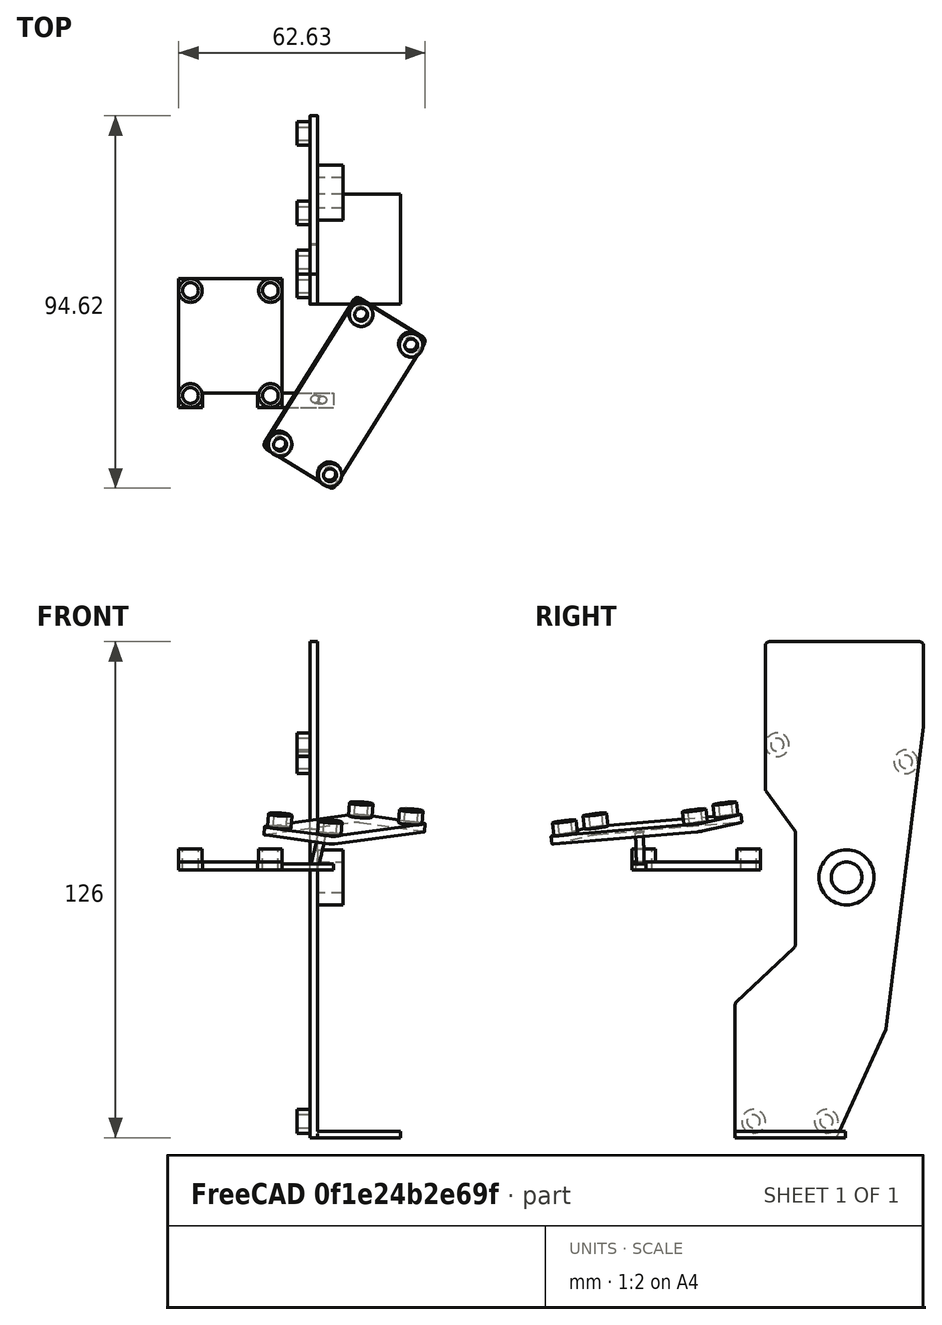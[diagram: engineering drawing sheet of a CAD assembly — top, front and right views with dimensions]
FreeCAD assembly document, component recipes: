
FREECAD ASSEMBLY — COMPONENT RECIPES ("case-vertical")

This assembly document has 10 components, labeled P0..P9 below (a component is one placed body or linked part). 8 of them carry a construction recipe — the FreeCAD feature program that regenerates the part from scratch, quoted from this document or its linked companion documents; the rest are supplied as boundary geometry only. No exploded tour is included for this assembly.
COMPONENT P0 — geometry summary ("Joystick v6"; no construction recipe available for this part):
  bounding box: 33.2 x 26.8 x 24.7 mm
  tessellated surface: 35,946 triangles
  volume: 4886 mm^3 (22% of its bounding box)
COMPONENT P1 — recipe-attached ("Part001", modeled in this document).
Construction recipe (the document's own serialized feature program — sketch geometry with constraints, then the solid features built on it; lengths are millimeters unless a unit is written):

FEATURE [Sketcher::SketchObject] PCB_Sketch_f9e4  label="left"
  ArcFitTolerance = 1e-06
  FullyConstrained = false
  MakeInternals = false
  MapMode = 5
  Placement = pos=(0,0,0) rot=(0,-1,0;1.5708rad)
  sketch-geometry (21):
    g0: LineSegment StartX=48.9342 StartY=15.25 StartZ=0 EndX=77.5946 EndY=15.25 EndZ=0
    g1: LineSegment StartX=27.2503 StartY=38.2054 StartZ=0 EndX=0.583058 EndY=26.0175 EndZ=0
    g2: LineSegment StartX=126 StartY=8.65 StartZ=0 EndX=126 EndY=45.95 EndZ=0
    g3: LineSegment StartX=9e-16 StartY=25.1085 StartZ=0 EndX=0 EndY=1 EndZ=0
    g4: LineSegment StartX=104.439 StartY=47.8424 StartZ=0 EndX=27.5489 EndY=38.289 EndZ=0
    g5: LineSegment StartX=34.5465 StartY=0.317255 StartZ=0 EndX=48.2035 EndY=14.9327 EndZ=0
    g6: LineSegment StartX=104.562 StartY=47.85 StartZ=0 EndX=125 EndY=47.85 EndZ=0
    g7: LineSegment StartX=125 StartY=7.65 StartZ=0 EndX=88.6266 EndY=7.65 EndZ=0
    g8: LineSegment StartX=1 StartY=1e-16 StartZ=0 EndX=33.8158 EndY=-1.6e-15 EndZ=0
    g9: LineSegment StartX=126 StartY=45.95 StartZ=0 EndX=126 EndY=46.85 EndZ=0
    g10: LineSegment StartX=78.291 StartY=14.9676 StartZ=0 EndX=88.0364 EndY=7.84274 EndZ=0
    g11: ArcOfCircle CenterX=27.666 CenterY=37.2959 CenterZ=0 NormalX=0 NormalY=0 NormalZ=-1 AngleXU=1.14211 Radius=1.00001 StartAngle=0 EndAngle=0.311303
    g12: ArcOfCircle CenterX=33.8158 CenterY=1.00002 CenterZ=0 NormalX=0 NormalY=0 NormalZ=-1 AngleXU=-2.39007 Radius=1.00002 StartAngle=0 EndAngle=0.81927
    g13: ArcOfCircle CenterX=48.9342 CenterY=14.25 CenterZ=0 NormalX=0 NormalY=0 NormalZ=-1 AngleXU=0.75152 Radius=1.00002 StartAngle=0 EndAngle=0.81927
    g14: ArcOfCircle CenterX=125 CenterY=46.85 CenterZ=0 NormalX=0 NormalY=0 NormalZ=-1 AngleXU=1.5708 Radius=0.999999 StartAngle=0 EndAngle=1.5708
    g15: ArcOfCircle CenterX=125 CenterY=8.65 CenterZ=0 NormalX=0 NormalY=0 NormalZ=-1 AngleXU=3.14159 Radius=0.999999 StartAngle=0 EndAngle=1.5708
    g16: ArcOfCircle CenterX=88.6266 CenterY=8.65 CenterZ=0 NormalX=0 NormalY=0 NormalZ=-1 AngleXU=-1.57079 Radius=1 StartAngle=0 EndAngle=0.631296
    g17: ArcOfCircle CenterX=104.562 CenterY=46.8498 CenterZ=0 NormalX=0 NormalY=0 NormalZ=-1 AngleXU=1.44719 Radius=1.00016 StartAngle=0 EndAngle=0.123594
    g18: ArcOfCircle CenterX=0.999999 CenterY=0.999999 CenterZ=0 NormalX=0 NormalY=0 NormalZ=-1 AngleXU=-1.5708 Radius=0.999999 StartAngle=0 EndAngle=1.5708
    g19: ArcOfCircle CenterX=1.00007 CenterY=25.1085 CenterZ=0 NormalX=0 NormalY=0 NormalZ=-1 AngleXU=4.52044e-05 Radius=1.00007 StartAngle=0 EndAngle=1.14063
    g20: ArcOfCircle CenterX=77.5946 CenterY=14.25 CenterZ=0 NormalX=0 NormalY=0 NormalZ=-1 AngleXU=1.57078 Radius=0.999961 StartAngle=0 EndAngle=0.770416
  constraints (21):
    c: Coincident(g3,g18)
    c: Coincident(g3,g19)
    c: Coincident(g1,g19)
    c: Coincident(g8,g18)
    c: Coincident(g1,g11)
    c: Coincident(g4,g11)
    c: Coincident(g8,g12)
    c: Coincident(g5,g12)
    c: Coincident(g5,g13)
    c: Coincident(g0,g13)
    c: Coincident(g0,g20)
    c: Coincident(g10,g20)
    c: Coincident(g10,g16)
    c: Coincident(g7,g16)
    c: Coincident(g4,g17)
    c: Coincident(g6,g17)
    c: Coincident(g7,g15)
    c: Coincident(g6,g14)
    c: Coincident(g2,g15)
    c: Coincident(g2,g9)
    c: Coincident(g9,g14)
FEATURE [PartDesign::Pad] Pad
  Direction = (-1,0,2e-16)
  Length = 2
  Length2 = 10
  Placement = pos=(0,0,0) rot=(0,-1,0;1.5708rad)
  Profile = -> PCB_Sketch_f9e4
  ReferenceAxis = -> PCB_Sketch_f9e4 [N_Axis]
  Refine = true
  Suppressed = false
  Type = 0
FEATURE [Sketcher::SketchObject] PCB_Sketch_f9e005  label="left holes"
  ArcFitTolerance = 1e-06
  AttachmentSupport = -> [Pad]
  FullyConstrained = false
  MakeInternals = false
  MapMode = 5
  Placement = pos=(-2,0,4e-16) rot=(0,-1,0;1.5708rad)
  sketch-geometry (8):
    g0: Circle CenterX=4.15 CenterY=23.1667 CenterZ=0 NormalX=0 NormalY=0 NormalZ=1 AngleXU=0 Radius=3
    g1: Circle CenterX=4.15 CenterY=4.65 CenterZ=0 NormalX=0 NormalY=0 NormalZ=1 AngleXU=0 Radius=3
    g2: Circle CenterX=95.5 CenterY=43.35 CenterZ=0 NormalX=0 NormalY=0 NormalZ=1 AngleXU=0 Radius=3
    g3: Circle CenterX=99.8333 CenterY=10.6833 CenterZ=0 NormalX=0 NormalY=0 NormalZ=1 AngleXU=0 Radius=3
    g4: Circle CenterX=95.5 CenterY=43.35 CenterZ=0 NormalX=0 NormalY=0 NormalZ=1 AngleXU=0 Radius=1.65
    g5: Circle CenterX=99.8333 CenterY=10.6833 CenterZ=0 NormalX=0 NormalY=0 NormalZ=1 AngleXU=0 Radius=1.65
    g6: Circle CenterX=4.15 CenterY=23.1667 CenterZ=0 NormalX=0 NormalY=0 NormalZ=1 AngleXU=0 Radius=1.65
    g7: Circle CenterX=4.15 CenterY=4.65 CenterZ=0 NormalX=0 NormalY=0 NormalZ=1 AngleXU=0 Radius=1.65
  constraints (12):
    c: Diameter(g0) = 6
    c: Diameter(g1) = 6
    c: Diameter(g2) = 6
    c: Diameter(g3) = 6
    c: Diameter(g4) = 3.3
    c: Coincident(g4,g2)
    c: Diameter(g5) = 3.3
    c: Coincident(g5,g3)
    c: Diameter(g6) = 3.3
    c: Coincident(g6,g0)
    c: Diameter(g7) = 3.3
    c: Coincident(g7,g1)
FEATURE [PartDesign::Pad] Pad003
  BaseFeature = -> Pad
  Direction = (-1,0,2e-16)
  Length = 3.3
  Length2 = 10
  Placement = pos=(0,0,0) rot=(0,-1,0;1.5708rad)
  Profile = -> PCB_Sketch_f9e005
  ReferenceAxis = -> PCB_Sketch_f9e005 [N_Axis]
  Refine = true
  Suppressed = false
  Type = 0
FEATURE [Sketcher::SketchObject] Sketch  label="tindie"
  ArcFitTolerance = 1e-06
  AttachmentSupport = -> [XY_Plane001]
  FullyConstrained = true
  MakeInternals = false
  MapMode = 5
  sketch-geometry (4):
    g0: LineSegment StartX=0 StartY=0 StartZ=0 EndX=21 EndY=0 EndZ=0
    g1: LineSegment StartX=21 StartY=0 StartZ=0 EndX=21 EndY=28 EndZ=0
    g2: LineSegment StartX=21 StartY=28 StartZ=0 EndX=0 EndY=28 EndZ=0
    g3: LineSegment StartX=0 StartY=28 StartZ=0 EndX=0 EndY=0 EndZ=0
  constraints (11):
    c: Coincident(g0,g1)
    c: Coincident(g1,g2)
    c: Coincident(g2,g3)
    c: Coincident(g3,g0)
    c: Horizontal(g0)
    c: Horizontal(g2)
    c: Vertical(g1)
    c: Vertical(g3)
    c: Coincident(g0,g-1)
    c: DistanceY(g1,g1) = 28
    c: DistanceX(g2,g2) = 21
FEATURE [Sketcher::SketchObject] PCB_Sketch_58ce002  label="thumb"
  ArcFitTolerance = 1e-06
  FullyConstrained = false
  MakeInternals = false
  sketch-geometry (8):
    g0: LineSegment StartX=21 StartY=44 StartZ=0 EndX=21 EndY=1 EndZ=0
    g1: LineSegment StartX=20 StartY=1e-16 StartZ=0 EndX=1 EndY=0 EndZ=0
    g2: LineSegment StartX=1 StartY=45 StartZ=0 EndX=20 EndY=45 EndZ=0
    g3: LineSegment StartX=1e-16 StartY=1 StartZ=0 EndX=3.3e-15 EndY=44 EndZ=0
    g4: ArcOfCircle CenterX=20 CenterY=44 CenterZ=0 NormalX=0 NormalY=0 NormalZ=-1 AngleXU=1.5708 Radius=0.999999 StartAngle=0 EndAngle=1.5708
    g5: ArcOfCircle CenterX=0.999999 CenterY=0.999999 CenterZ=0 NormalX=0 NormalY=0 NormalZ=-1 AngleXU=-1.5708 Radius=0.999999 StartAngle=0 EndAngle=1.5708
    g6: ArcOfCircle CenterX=20 CenterY=0.999999 CenterZ=0 NormalX=0 NormalY=0 NormalZ=-1 AngleXU=3.14159 Radius=0.999999 StartAngle=0 EndAngle=1.5708
    g7: ArcOfCircle CenterX=0.999999 CenterY=44 CenterZ=0 NormalX=0 NormalY=0 NormalZ=-1 AngleXU=-7.47076e-07 Radius=0.999999 StartAngle=0 EndAngle=1.5708
  constraints (8):
    c: Coincident(g3,g5)
    c: Coincident(g3,g7)
    c: Coincident(g1,g5)
    c: Coincident(g2,g7)
    c: Coincident(g1,g6)
    c: Coincident(g2,g4)
    c: Coincident(g0,g6)
    c: Coincident(g0,g4)
FEATURE [Sketcher::SketchObject] Sketch001  label="thumbstick pcb"
  ArcFitTolerance = 1e-06
  FullyConstrained = false
  MakeInternals = false
  sketch-geometry (8):
    g0: LineSegment [constr] StartX=2.54 StartY=29.21 StartZ=0 EndX=2.54 EndY=2.54 EndZ=0
    g1: LineSegment [constr] StartX=2.54 StartY=2.54 StartZ=0 EndX=22.86 EndY=2.54 EndZ=0
    g2: LineSegment [constr] StartX=22.86 StartY=2.54 StartZ=0 EndX=22.86 EndY=29.21 EndZ=0
    g3: LineSegment [constr] StartX=22.86 StartY=29.21 StartZ=0 EndX=2.54 EndY=29.21 EndZ=0
    g4: LineSegment StartX=-0.46 StartY=32.21 StartZ=0 EndX=-0.46 EndY=-0.46 EndZ=0
    g5: LineSegment StartX=-0.46 StartY=-0.46 StartZ=0 EndX=25.86 EndY=-0.46 EndZ=0
    g6: LineSegment StartX=25.86 StartY=-0.46 StartZ=0 EndX=25.86 EndY=32.21 EndZ=0
    g7: LineSegment StartX=25.86 StartY=32.21 StartZ=0 EndX=-0.46 EndY=32.21 EndZ=0
  constraints (20):
    c: Coincident(g0,g1)
    c: Coincident(g1,g2)
    c: Coincident(g2,g3)
    c: Coincident(g3,g0)
    c: Vertical(g0)
    c: Vertical(g2)
    c: Horizontal(g1)
    c: Horizontal(g3)
    c: Coincident(g4,g5)
    c: Coincident(g5,g6)
    c: Coincident(g6,g7)
    c: Coincident(g7,g4)
    c: Vertical(g4)
    c: Vertical(g6)
    c: Horizontal(g5)
    c: Horizontal(g7)
    c: Distance(g7,g3) = 3
    c: Distance(g5,g1) = 3
    c: Distance(g6,g2) = 3
    c: Distance(g4,g0) = 3
FEATURE [PartDesign::Pad] Pad009
  Direction = (0,0,1)
  Length = 2
  Length2 = 10
  Profile = -> Sketch001
  ReferenceAxis = -> Sketch001 [N_Axis]
  Refine = true
  Suppressed = false
  Type = 0
FEATURE [Sketcher::SketchObject] Sketch004  label="thumbstick holes"
  ArcFitTolerance = 1e-06
  AttacherType = Attacher::AttachEngine3D
  AttachmentSupport = -> [Pad009]
  FullyConstrained = false
  MakeInternals = false
  MapMode = 5
  Placement = pos=(0,0,2) rot=(0,0,1;0rad)
  sketch-geometry (8):
    g0: Circle CenterX=2.54 CenterY=29.21 CenterZ=0 NormalX=0 NormalY=0 NormalZ=1 AngleXU=0 Radius=3
    g1: Circle CenterX=22.86 CenterY=29.21 CenterZ=0 NormalX=0 NormalY=0 NormalZ=1 AngleXU=0 Radius=3
    g2: Circle CenterX=22.86 CenterY=2.54 CenterZ=0 NormalX=0 NormalY=0 NormalZ=1 AngleXU=0 Radius=3
    g3: Circle CenterX=2.54 CenterY=2.54 CenterZ=0 NormalX=0 NormalY=0 NormalZ=1 AngleXU=0 Radius=3
    g4: Circle CenterX=2.54 CenterY=29.21 CenterZ=0 NormalX=0 NormalY=0 NormalZ=1 AngleXU=0 Radius=2
    g5: Circle CenterX=22.86 CenterY=29.21 CenterZ=0 NormalX=0 NormalY=0 NormalZ=1 AngleXU=0 Radius=2
    g6: Circle CenterX=22.86 CenterY=2.54 CenterZ=0 NormalX=0 NormalY=0 NormalZ=1 AngleXU=0 Radius=2
    g7: Circle CenterX=2.54 CenterY=2.54 CenterZ=0 NormalX=0 NormalY=0 NormalZ=1 AngleXU=0 Radius=2
  constraints (12):
    c: Diameter(g0) = 6
    c: Diameter(g1) = 6
    c: Diameter(g2) = 6
    c: Diameter(g3) = 6
    c: Diameter(g4) = 4
    c: Coincident(g4,g0)
    c: Diameter(g5) = 4
    c: Coincident(g5,g1)
    c: Diameter(g6) = 4
    c: Coincident(g6,g2)
    c: Diameter(g7) = 4
    c: Coincident(g7,g3)
FEATURE [PartDesign::Pad] Pad010
  BaseFeature = -> Pad009
  Direction = (0,0,1)
  Length = 3.3
  Length2 = 10
  Profile = -> Sketch004
  ReferenceAxis = -> Sketch004 [N_Axis]
  Refine = true
  Suppressed = false
  Type = 0
FEATURE [PartDesign::Pad] Pad011
  Direction = (0,0,1)
  Length = 2
  Length2 = 10
  Profile = -> PCB_Sketch_58ce002
  ReferenceAxis = -> PCB_Sketch_58ce002 [N_Axis]
  Refine = true
  Suppressed = false
  Type = 0
FEATURE [Sketcher::SketchObject] PCB_Sketch_58ce001  label="thumb-holes"
  ArcFitTolerance = 1e-06
  AttacherType = Attacher::AttachEngine3D
  AttachmentSupport = -> [Pad011]
  FullyConstrained = false
  MakeInternals = false
  MapMode = 5
  Placement = pos=(0,0,2) rot=(0,0,1;0rad)
  sketch-geometry (8):
    g0: Circle CenterX=3 CenterY=42 CenterZ=0 NormalX=0 NormalY=0 NormalZ=1 AngleXU=0 Radius=3
    g1: Circle CenterX=18 CenterY=42 CenterZ=0 NormalX=0 NormalY=0 NormalZ=1 AngleXU=0 Radius=3
    g2: Circle CenterX=18 CenterY=3 CenterZ=0 NormalX=0 NormalY=0 NormalZ=1 AngleXU=0 Radius=3
    g3: Circle CenterX=3 CenterY=3 CenterZ=0 NormalX=0 NormalY=0 NormalZ=1 AngleXU=0 Radius=3
    g4: Circle CenterX=3 CenterY=42 CenterZ=0 NormalX=0 NormalY=0 NormalZ=1 AngleXU=0 Radius=1.65
    g5: Circle CenterX=18 CenterY=42 CenterZ=0 NormalX=0 NormalY=0 NormalZ=1 AngleXU=0 Radius=1.65
    g6: Circle CenterX=18 CenterY=3 CenterZ=0 NormalX=0 NormalY=0 NormalZ=1 AngleXU=0 Radius=1.65
    g7: Circle CenterX=3 CenterY=3 CenterZ=0 NormalX=0 NormalY=0 NormalZ=1 AngleXU=0 Radius=1.65
  constraints (12):
    c: Diameter(g0) = 6
    c: Diameter(g1) = 6
    c: Diameter(g2) = 6
    c: Diameter(g3) = 6
    c: Diameter(g4) = 3.3
    c: Coincident(g4,g0)
    c: Diameter(g5) = 3.3
    c: Coincident(g5,g1)
    c: Diameter(g6) = 3.3
    c: Coincident(g6,g2)
    c: Diameter(g7) = 3.3
    c: Coincident(g7,g3)
FEATURE [PartDesign::Pad] Pad012
  BaseFeature = -> Pad011
  Direction = (0,0,1)
  Length = 3.3
  Length2 = 10
  Profile = -> PCB_Sketch_58ce001
  ReferenceAxis = -> PCB_Sketch_58ce001 [N_Axis]
  Refine = true
  Suppressed = false
  Type = 0
FEATURE [Sketcher::SketchObject] Sketch006
  ArcFitTolerance = 1e-06
  AttachmentSupport = -> [Pad010]
  FullyConstrained = false
  MakeInternals = false
  MapMode = 5
  Placement = pos=(-0.46,0,0) rot=(0.57735,-0.57735,-0.57735;2.0944rad)
  sketch-geometry (4):
    g0: LineSegment StartX=-32.2214 StartY=1.56343 StartZ=0 EndX=-32.2214 EndY=0 EndZ=0
    g1: LineSegment StartX=-32.2214 StartY=0 StartZ=0 EndX=-28.6163 EndY=0 EndZ=0
    g2: LineSegment StartX=-28.6163 StartY=0 StartZ=0 EndX=-28.6163 EndY=1.56343 EndZ=0
    g3: LineSegment StartX=-28.6163 StartY=1.56343 StartZ=0 EndX=-32.2214 EndY=1.56343 EndZ=0
  constraints (9):
    c: Coincident(g0,g1)
    c: Coincident(g1,g2)
    c: Coincident(g2,g3)
    c: Coincident(g3,g0)
    c: Vertical(g0)
    c: Vertical(g2)
    c: Horizontal(g1)
    c: Horizontal(g3)
    c: PointOnObject(g1,g-1)
FEATURE [PartDesign::Pad] Pad013
  BaseFeature = -> Pad010
  Direction = (-1,0,0)
  Length = 13
  Length2 = 10
  Profile = -> Sketch006
  ReferenceAxis = -> Sketch006 [N_Axis]
  Refine = true
  Suppressed = false
  Type = 0
FEATURE [Sketcher::SketchObject] Sketch007
  ArcFitTolerance = 1e-06
  AttachmentSupport = -> [Pad013]
  FullyConstrained = true
  MakeInternals = false
  MapMode = 5
  Placement = pos=(0,0,1.56343) rot=(0,0,1;0rad)
FEATURE [Sketcher::SketchObject] Sketch008
  ArcFitTolerance = 1e-06
  AttachmentSupport = -> [Pad012]
  FullyConstrained = false
  MakeInternals = false
  MapMode = 5
  Placement = pos=(0,0,0) rot=(1,0,0;3.14159rad)
  sketch-geometry (1):
    g0: Circle CenterX=6.77488 CenterY=-17.9445 CenterZ=0 NormalX=0 NormalY=0 NormalZ=1 AngleXU=0 Radius=1
  constraints (1):
    c: Diameter(g0) = 2
FEATURE [PartDesign::Pad] Pad014
  BaseFeature = -> Pad012
  Direction = (-0.6,-1.1,-6.5)
  Length = 8.2
  Length2 = 10
  Profile = -> Sketch008
  ReferenceAxis = -> Sketch008 [N_Axis]
  Refine = true
  Suppressed = false
  Type = 0
  UseCustomVector = true
FEATURE [PartDesign::Body] Body001  label="Thumb"
  AllowCompound = false
  Group = -> [PCB_Sketch_58ce002,PCB_Sketch_58ce001,Pad011,Pad012,Sketch008,Pad014]
  Origin = -> Origin002
  Placement = pos=(-14,-36,77) rot=(-0.86,-0.79,4.6;5.71246rad)
  Tip = -> Pad014
FEATURE [Sketcher::SketchObject] Sketch015
  ArcFitTolerance = 1e-06
  AttachmentSupport = -> [Pad013]
  ExternalGeometry = -> [Pad013]
  FullyConstrained = true
  MakeInternals = false
  MapMode = 5
  Placement = pos=(0,0,5.3) rot=(0,0,1;0rad)
  sketch-geometry (4):
    g0: Circle CenterX=2.54 CenterY=29.21 CenterZ=0 NormalX=0 NormalY=0 NormalZ=1 AngleXU=0 Radius=2
    g1: Circle CenterX=22.86 CenterY=29.21 CenterZ=0 NormalX=0 NormalY=0 NormalZ=1 AngleXU=0 Radius=2
    g2: Circle CenterX=22.86 CenterY=2.54 CenterZ=0 NormalX=0 NormalY=0 NormalZ=1 AngleXU=0 Radius=2
    g3: Circle CenterX=2.54 CenterY=2.54 CenterZ=0 NormalX=0 NormalY=0 NormalZ=1 AngleXU=0 Radius=2
  constraints (8):
    c: Coincident(g0,g-3)
    c: Equal(g0,g-3)
    c: Coincident(g1,g-4)
    c: Equal(g1,g-4)
    c: Coincident(g2,g-5)
    c: Equal(g2,g-5)
    c: Coincident(g3,g-6)
    c: Equal(g3,g-6)
FEATURE [PartDesign::Pocket] Pocket
  BaseFeature = -> Pad013
  Direction = (0,0,-1)
  Length = 6
  Length2 = 5
  Profile = -> Sketch015
  ReferenceAxis = -> Sketch015 [N_Axis]
  Refine = true
  Suppressed = false
  Type = 1
FEATURE [Sketcher::SketchObject] Sketch016
  ArcFitTolerance = 1e-06
  AttachmentSupport = -> [Pocket]
  ExternalGeometry = -> [Pocket]
  FullyConstrained = false
  MakeInternals = false
  MapMode = 5
  Placement = pos=(0,0,2) rot=(0,0,1;0rad)
  sketch-geometry (4):
    g0: LineSegment StartX=5.79831 StartY=32.21 StartZ=0 EndX=5.79831 EndY=28.6463 EndZ=0
    g1: LineSegment StartX=5.79831 StartY=28.6463 StartZ=0 EndX=19.7769 EndY=28.6463 EndZ=0
    g2: LineSegment StartX=19.7769 StartY=28.6463 StartZ=0 EndX=19.7769 EndY=32.21 EndZ=0
    g3: LineSegment StartX=19.7769 StartY=32.21 StartZ=0 EndX=5.79831 EndY=32.21 EndZ=0
  constraints (9):
    c: Coincident(g0,g1)
    c: Coincident(g1,g2)
    c: Coincident(g2,g3)
    c: Coincident(g3,g0)
    c: Vertical(g0)
    c: Vertical(g2)
    c: Horizontal(g1)
    c: Horizontal(g3)
    c: PointOnObject(g0,g-3)
FEATURE [PartDesign::Pocket] Pocket001
  BaseFeature = -> Pocket
  Direction = (0,0,-1)
  Length = 5
  Length2 = 5
  Profile = -> Sketch016
  ReferenceAxis = -> Sketch016 [N_Axis]
  Refine = true
  Suppressed = false
  Type = 1
FEATURE [PartDesign::Body] Body002  label="Thumbstick"
  AllowCompound = false
  Group = -> [Sketch004,Sketch001,Pad009,Pad010,Sketch006,Pad013,Sketch007,Sketch015,Pocket,Sketch016,Pocket001]
  Origin = -> Origin003
  Placement = pos=(-9.46,6,68) rot=(0,0,1;3.14159rad)
  Tip = -> Pocket001
FEATURE [PartDesign::Pad] Pad015
  BaseFeature = -> Pad003
  Direction = (0,0,1)
  Length = 1.6
  Length2 = 10
  Placement = pos=(0,0,0) rot=(0,-1,0;1.5708rad)
  Profile = -> Sketch
  ReferenceAxis = -> Sketch [N_Axis]
  Refine = true
  Suppressed = false
  Type = 0
FEATURE [Sketcher::SketchObject] Sketch017
  ArcFitTolerance = 1e-06
  AttachmentSupport = -> [Pad015]
  FullyConstrained = false
  MakeInternals = false
  MapMode = 5
  Placement = pos=(1e-16,0,0) rot=(0.707107,0,0.707107;3.14159rad)
  sketch-geometry (2):
    g0: Circle CenterX=66.1396 CenterY=-28.2921 CenterZ=0 NormalX=0 NormalY=0 NormalZ=1 AngleXU=0 Radius=3.9
    g1: Circle CenterX=66.1396 CenterY=-28.2921 CenterZ=0 NormalX=0 NormalY=0 NormalZ=1 AngleXU=0 Radius=7
  constraints (3):
    c: Diameter(g0) = 7.8
    c: Diameter(g1) = 14
    c: Coincident(g1,g0)
FEATURE [PartDesign::Pad] Pad016
  BaseFeature = -> Pad015
  Direction = (1,0,-2e-16)
  Length = 6.5
  Length2 = 10
  Placement = pos=(0,0,0) rot=(0,-1,0;1.5708rad)
  Profile = -> Sketch017
  ReferenceAxis = -> Sketch017 [N_Axis]
  Refine = true
  Suppressed = false
  Type = 0
FEATURE [PartDesign::Body] Body  label="Left"
  AllowCompound = true
  Group = -> [PCB_Sketch_f9e005,PCB_Sketch_f9e4,Pad,Pad003,Sketch,Pad015,Sketch017,Pad016]
  Origin = -> Origin001
  Tip = -> Pad016
COMPONENT P2 — same part as P1; its construction recipe is shown at P1.
COMPONENT P3 — geometry summary ("left001"; no construction recipe available for this part):
  bounding box: 126.7 x 48.0 x 12.9 mm
  tessellated surface: 117,438 triangles
  volume: 8489 mm^3 (11% of its bounding box)
COMPONENT P4 — recipe-attached ("stem", modeled in this document).
Construction recipe (the document's own serialized feature program — sketch geometry with constraints, then the solid features built on it; lengths are millimeters unless a unit is written):

FEATURE [Sketcher::SketchObject] PCB_Sketch_58ce002  label="thumb"
  ArcFitTolerance = 1e-06
  FullyConstrained = false
  MakeInternals = false
  sketch-geometry (8):
    g0: LineSegment StartX=21 StartY=44 StartZ=0 EndX=21 EndY=1 EndZ=0
    g1: LineSegment StartX=20 StartY=1e-16 StartZ=0 EndX=1 EndY=0 EndZ=0
    g2: LineSegment StartX=1 StartY=45 StartZ=0 EndX=20 EndY=45 EndZ=0
    g3: LineSegment StartX=1e-16 StartY=1 StartZ=0 EndX=3.3e-15 EndY=44 EndZ=0
    g4: ArcOfCircle CenterX=20 CenterY=44 CenterZ=0 NormalX=0 NormalY=0 NormalZ=-1 AngleXU=1.5708 Radius=0.999999 StartAngle=0 EndAngle=1.5708
    g5: ArcOfCircle CenterX=0.999999 CenterY=0.999999 CenterZ=0 NormalX=0 NormalY=0 NormalZ=-1 AngleXU=-1.5708 Radius=0.999999 StartAngle=0 EndAngle=1.5708
    g6: ArcOfCircle CenterX=20 CenterY=0.999999 CenterZ=0 NormalX=0 NormalY=0 NormalZ=-1 AngleXU=3.14159 Radius=0.999999 StartAngle=0 EndAngle=1.5708
    g7: ArcOfCircle CenterX=0.999999 CenterY=44 CenterZ=0 NormalX=0 NormalY=0 NormalZ=-1 AngleXU=-7.47076e-07 Radius=0.999999 StartAngle=0 EndAngle=1.5708
  constraints (8):
    c: Coincident(g3,g5)
    c: Coincident(g3,g7)
    c: Coincident(g1,g5)
    c: Coincident(g2,g7)
    c: Coincident(g1,g6)
    c: Coincident(g2,g4)
    c: Coincident(g0,g6)
    c: Coincident(g0,g4)
FEATURE [PartDesign::Pad] Pad011
  Direction = (0,0,1)
  Length = 2
  Length2 = 10
  Profile = -> PCB_Sketch_58ce002
  ReferenceAxis = -> PCB_Sketch_58ce002 [N_Axis]
  Refine = true
  Suppressed = false
  Type = 0
FEATURE [Sketcher::SketchObject] PCB_Sketch_58ce001  label="thumb-holes"
  ArcFitTolerance = 1e-06
  AttacherType = Attacher::AttachEngine3D
  AttachmentSupport = -> [Pad011]
  FullyConstrained = false
  MakeInternals = false
  MapMode = 5
  Placement = pos=(0,0,2) rot=(0,0,1;0rad)
  sketch-geometry (8):
    g0: Circle CenterX=3 CenterY=42 CenterZ=0 NormalX=0 NormalY=0 NormalZ=1 AngleXU=0 Radius=3
    g1: Circle CenterX=18 CenterY=42 CenterZ=0 NormalX=0 NormalY=0 NormalZ=1 AngleXU=0 Radius=3
    g2: Circle CenterX=18 CenterY=3 CenterZ=0 NormalX=0 NormalY=0 NormalZ=1 AngleXU=0 Radius=3
    g3: Circle CenterX=3 CenterY=3 CenterZ=0 NormalX=0 NormalY=0 NormalZ=1 AngleXU=0 Radius=3
    g4: Circle CenterX=3 CenterY=42 CenterZ=0 NormalX=0 NormalY=0 NormalZ=1 AngleXU=0 Radius=1.65
    g5: Circle CenterX=18 CenterY=42 CenterZ=0 NormalX=0 NormalY=0 NormalZ=1 AngleXU=0 Radius=1.65
    g6: Circle CenterX=18 CenterY=3 CenterZ=0 NormalX=0 NormalY=0 NormalZ=1 AngleXU=0 Radius=1.65
    g7: Circle CenterX=3 CenterY=3 CenterZ=0 NormalX=0 NormalY=0 NormalZ=1 AngleXU=0 Radius=1.65
  constraints (12):
    c: Diameter(g0) = 6
    c: Diameter(g1) = 6
    c: Diameter(g2) = 6
    c: Diameter(g3) = 6
    c: Diameter(g4) = 3.3
    c: Coincident(g4,g0)
    c: Diameter(g5) = 3.3
    c: Coincident(g5,g1)
    c: Diameter(g6) = 3.3
    c: Coincident(g6,g2)
    c: Diameter(g7) = 3.3
    c: Coincident(g7,g3)
FEATURE [PartDesign::Pad] Pad012
  BaseFeature = -> Pad011
  Direction = (0,0,1)
  Length = 3.3
  Length2 = 10
  Profile = -> PCB_Sketch_58ce001
  ReferenceAxis = -> PCB_Sketch_58ce001 [N_Axis]
  Refine = true
  Suppressed = false
  Type = 0
FEATURE [Sketcher::SketchObject] Sketch008
  ArcFitTolerance = 1e-06
  AttachmentSupport = -> [Pad012]
  FullyConstrained = false
  MakeInternals = false
  MapMode = 5
  Placement = pos=(0,0,0) rot=(1,0,0;3.14159rad)
  sketch-geometry (1):
    g0: Circle CenterX=6.77488 CenterY=-17.9445 CenterZ=0 NormalX=0 NormalY=0 NormalZ=1 AngleXU=0 Radius=1
  constraints (1):
    c: Diameter(g0) = 2
FEATURE [PartDesign::Pad] Pad014
  BaseFeature = -> Pad012
  Direction = (-0.6,-1.1,-6.5)
  Length = 8.2
  Length2 = 10
  Profile = -> Sketch008
  ReferenceAxis = -> Sketch008 [N_Axis]
  Refine = true
  Suppressed = false
  Type = 0
  UseCustomVector = true
FEATURE [PartDesign::Body] Body001  label="Thumb"
  AllowCompound = false
  Group = -> [PCB_Sketch_58ce002,PCB_Sketch_58ce001,Pad011,Pad012,Sketch008,Pad014]
  Origin = -> Origin002
  Placement = pos=(-14,-36,77) rot=(-0.86,-0.79,4.6;5.71246rad)
  Tip = -> Pad014
COMPONENT P5 — same part as P4; its construction recipe is shown at P4.
COMPONENT P6 — recipe-attached ("thumb-cluster", a linked part whose construction recipe lives in a companion FreeCAD document of the same project; that document's serialized recipe follows).
Construction recipe (the companion document, serialized — sketch geometry with constraints, then the solid features built on it; lengths are millimeters unless a unit is written):

FCSTD DOCUMENT  (FreeCAD 1.0RUnknown)
Label: thumb-cluster
License: All rights reserved
LicenseURL: https://en.wikipedia.org/wiki/All_rights_reserved
objects: Part::Feature×14, Sketcher::SketchObject×10, App::Link×10, App::Part×6, PartDesign::Pocket×4, PartDesign::Pad×3, PartDesign::Chamfer×3, PartDesign::Thickness×2, PartDesign::Body×2, PartDesign::SubShapeBinder×2, PartDesign::CoordinateSystem×1, PartDesign::ShapeBinder×1
note: 76 computed .brp shape members not serialized (recipe doc carries the construction recipe); baked Part::Feature solids carry a one-line shape summary decoded from their .brp

FEATURE [PartDesign::CoordinateSystem] Local_CS_58ce
  AttacherType = Attacher::AttachEngine3D
  MapMode = 2
FEATURE [Part::Feature] Pcb_58ce
  Placement = pos=(-19.5,69,0) rot=(0,0,1;0rad)
  shape: bbox 21 x 45 x 1.6 mm, 50 faces (baked)
FEATURE [Sketcher::SketchObject] PCB_Sketch_58ce
  ArcFitTolerance = 1e-06
  FullyConstrained = false
  MakeInternals = false
  sketch-geometry (8):
    g0: LineSegment StartX=21 StartY=44 StartZ=0 EndX=21 EndY=1 EndZ=0
    g1: LineSegment StartX=20 StartY=1e-16 StartZ=0 EndX=1 EndY=0 EndZ=0
    g2: LineSegment StartX=1 StartY=45 StartZ=0 EndX=20 EndY=45 EndZ=0
    g3: LineSegment StartX=1e-16 StartY=1 StartZ=0 EndX=3.3e-15 EndY=44 EndZ=0
    g4: ArcOfCircle CenterX=20 CenterY=44 CenterZ=0 NormalX=0 NormalY=0 NormalZ=-1 AngleXU=1.5708 Radius=0.999999 StartAngle=0 EndAngle=1.5708
    g5: ArcOfCircle CenterX=0.999999 CenterY=0.999999 CenterZ=0 NormalX=0 NormalY=0 NormalZ=-1 AngleXU=-1.5708 Radius=0.999999 StartAngle=0 EndAngle=1.5708
    g6: ArcOfCircle CenterX=20 CenterY=0.999999 CenterZ=0 NormalX=0 NormalY=0 NormalZ=-1 AngleXU=3.14159 Radius=0.999999 StartAngle=0 EndAngle=1.5708
    g7: ArcOfCircle CenterX=0.999999 CenterY=44 CenterZ=0 NormalX=0 NormalY=0 NormalZ=-1 AngleXU=-7.47076e-07 Radius=0.999999 StartAngle=0 EndAngle=1.5708
  constraints (8):
    c: Coincident(g3,g5)
    c: Coincident(g3,g7)
    c: Coincident(g1,g5)
    c: Coincident(g2,g7)
    c: Coincident(g1,g6)
    c: Coincident(g2,g4)
    c: Coincident(g0,g6)
    c: Coincident(g0,g4)
FEATURE [App::Part] Board_Geoms_58ce
  Group = -> [Pcb_58ce,PCB_Sketch_58ce]
  Origin = -> Origin
FEATURE [Part::Feature] Shape  label="D24_D_SOD_123_0f779e6ff9e7"
  Placement = pos=(3.66673,13.8333,0) rot=(0,0,-1;0.785398rad)
  shape: bbox 3.147 x 3.147 x 1.25 mm, 67 faces (baked)
FEATURE [Part::Feature] Shape001  label="J4_SOLID_42e36dcc9d63"
  Placement = pos=(10.9645,42.4,0) rot=(0,0.707107,0.707107;3.14159rad)
  shape: bbox 5.501 x 4.001 x 0.9009 mm, 979 faces (baked)
FEATURE [App::Link] D24_D_SOD_123_0f779e6ff9e7_ln_  label="D23_D_SOD_123_3fd67df90355"
  LinkPlacement = pos=(5.66673,15.8333,0) rot=(0,0,-1;0.785398rad)
  LinkedObject = -> Shape
  Placement = pos=(5.66673,15.8333,0) rot=(0,0,-1;0.785398rad)
FEATURE [App::Link] D24_D_SOD_123_0f779e6ff9e7_ln_001  label="D30_D_SOD_123_61e72e2af53f"
  LinkPlacement = pos=(19.75,16.55,0) rot=(0,0,-1;1.5708rad)
  LinkedObject = -> Shape
  Placement = pos=(19.75,16.55,0) rot=(0,0,-1;1.5708rad)
FEATURE [App::Link] D24_D_SOD_123_0f779e6ff9e7_ln_002  label="D27_D_SOD_123_7b2efe9b5669"
  LinkPlacement = pos=(17.6667,24.3333,0) rot=(0,0,1;2.35619rad)
  LinkedObject = -> Shape
  Placement = pos=(17.6667,24.3333,0) rot=(0,0,1;2.35619rad)
FEATURE [App::Link] D24_D_SOD_123_0f779e6ff9e7_ln_003  label="D22_D_SOD_123_057a97edfa83"
  LinkPlacement = pos=(7.66673,17.8333,0) rot=(0,0,-1;0.785398rad)
  LinkedObject = -> Shape
  Placement = pos=(7.66673,17.8333,0) rot=(0,0,-1;0.785398rad)
FEATURE [App::Link] D24_D_SOD_123_0f779e6ff9e7_ln_004  label="D29_D_SOD_123_cdf521000048"
  LinkPlacement = pos=(16.5,16.55,0) rot=(0,0,-1;1.5708rad)
  LinkedObject = -> Shape
  Placement = pos=(16.5,16.55,0) rot=(0,0,-1;1.5708rad)
FEATURE [App::Link] D24_D_SOD_123_0f779e6ff9e7_ln_005  label="D28_D_SOD_123_d5d7d507dfc1"
  LinkPlacement = pos=(15.6667,22.3333,0) rot=(0,0,1;2.35619rad)
  LinkedObject = -> Shape
  Placement = pos=(15.6667,22.3333,0) rot=(0,0,1;2.35619rad)
FEATURE [App::Link] D24_D_SOD_123_0f779e6ff9e7_ln_006  label="D20_D_SOD_123_675b5f77a9ad"
  LinkPlacement = pos=(5.16673,33.8333,0) rot=(0,0,-1;0.785398rad)
  LinkedObject = -> Shape
  Placement = pos=(5.16673,33.8333,0) rot=(0,0,-1;0.785398rad)
FEATURE [Part::Feature] Part__Feature  label="SKRHAD"
  shape: bbox 7.483 x 7.5 x 5.5 mm, 242 faces (baked)
FEATURE [Part::Feature] Part__Feature001  label="Pins"
  shape: bbox 1.15 x 0.8 x 0.1 mm, 6 faces (baked)
FEATURE [Part::Feature] Part__Feature002  label="Pins001"
  shape: bbox 1.15 x 0.8 x 0.1 mm, 6 faces (baked)
FEATURE [Part::Feature] Part__Feature003  label="Pins002"
  shape: bbox 1.15 x 0.8 x 0.1 mm, 6 faces (baked)
FEATURE [Part::Feature] Part__Feature004  label="Pins003"
  shape: bbox 1.15 x 0.8 x 0.1 mm, 6 faces (baked)
FEATURE [Part::Feature] Part__Feature005  label="Pins004"
  shape: bbox 1.15 x 0.8 x 0.1 mm, 6 faces (baked)
FEATURE [Part::Feature] Part__Feature006  label="Pins005"
  shape: bbox 1.15 x 0.8 x 0.1 mm, 6 faces (baked)
FEATURE [Part::Feature] Part__Feature007  label="Pins006"
  shape: bbox 1.64 x 1.44 x 0.1 mm, 6 faces (baked)
FEATURE [Part::Feature] Part__Feature008  label="Pins007"
  shape: bbox 1.64 x 1.44 x 0.1 mm, 6 faces (baked)
FEATURE [Part::Feature] Part__Feature009  label="Lugs"
  shape: bbox 0.55 x 0.55 x 1.8 mm, 3 faces (baked)
FEATURE [Part::Feature] Part__Feature010  label="Lugs001"
  shape: bbox 0.85 x 0.85 x 1.8 mm, 3 faces (baked)
FEATURE [App::Part] SKRHADE  label="S6_SKRHADE_66ce9957abdd"
  Group = -> [Part__Feature,Part__Feature001,Part__Feature002,Part__Feature003,Part__Feature004,Part__Feature005,Part__Feature006,Part__Feature007,Part__Feature008,Part__Feature009,Part__Feature010]
  Origin = -> Origin008
  Placement = pos=(10.9645,9.96447,0) rot=(0,0,-1;0.785398rad)
FEATURE [App::Link] D24_D_SOD_123_0f779e6ff9e7_ln_007  label="D21_D_SOD_123_014bcfdeeddd"
  LinkPlacement = pos=(3.16673,31.8333,0) rot=(0,0,-1;0.785398rad)
  LinkedObject = -> Shape
  Placement = pos=(3.16673,31.8333,0) rot=(0,0,-1;0.785398rad)
FEATURE [App::Link] D24_D_SOD_123_0f779e6ff9e7_ln_008  label="D19_D_SOD_123_2a26592c9c0c"
  LinkPlacement = pos=(7.16673,35.8333,0) rot=(0,0,-1;0.785398rad)
  LinkedObject = -> Shape
  Placement = pos=(7.16673,35.8333,0) rot=(0,0,-1;0.785398rad)
FEATURE [App::Link] S6_SKRHADE_66ce9957abdd_ln_  label="S5_SKRHADE_e4e283c67a98"
  LinkPlacement = pos=(10.9645,28.5203,0) rot=(0,0,-1;0.785398rad)
  LinkedObject = -> SKRHADE
  Placement = pos=(10.9645,28.5203,0) rot=(0,0,-1;0.785398rad)
FEATURE [App::Part] Top_58ce
  Group = -> [Shape,Shape001,D24_D_SOD_123_0f779e6ff9e7_ln_,D24_D_SOD_123_0f779e6ff9e7_ln_001,D24_D_SOD_123_0f779e6ff9e7_ln_002,D24_D_SOD_123_0f779e6ff9e7_ln_003,D24_D_SOD_123_0f779e6ff9e7_ln_004,D24_D_SOD_123_0f779e6ff9e7_ln_005,D24_D_SOD_123_0f779e6ff9e7_ln_006,SKRHADE,D24_D_SOD_123_0f779e6ff9e7_ln_007,D24_D_SOD_123_0f779e6ff9e7_ln_008,S6_SKRHADE_66ce9957abdd_ln_]
  Origin = -> Origin003
FEATURE [App::Part] Step_Models_58ce
  Group = -> [Top_58ce]
  Origin = -> Origin002
FEATURE [Sketcher::SketchObject] Sketch  label="2.2"
  ArcFitTolerance = 1e-06
  FullyConstrained = false
  MakeInternals = false
  Placement = pos=(0,0,0) rot=(0,0,1;3.14159rad)
  sketch-geometry (8):
    g0: LineSegment StartX=-23.2 StartY=-44 StartZ=0 EndX=-23.2 EndY=-0.999999 EndZ=0
    g1: ArcOfCircle CenterX=-20 CenterY=-0.999999 CenterZ=0 NormalX=0 NormalY=0 NormalZ=1 AngleXU=-3.14159 Radius=3.2 StartAngle=4.71239 EndAngle=6.28318
    g2: LineSegment StartX=-20 StartY=2.2 StartZ=0 EndX=-0.999999 EndY=2.2 EndZ=0
    g3: ArcOfCircle CenterX=-0.999999 CenterY=-0.999999 CenterZ=0 NormalX=0 NormalY=0 NormalZ=1 AngleXU=1.5708 Radius=3.2 StartAngle=4.71239 EndAngle=6.28318
    g4: LineSegment StartX=2.2 StartY=-0.999999 StartZ=0 EndX=2.2 EndY=-44 EndZ=0
    g5: ArcOfCircle CenterX=-0.999999 CenterY=-44 CenterZ=0 NormalX=0 NormalY=0 NormalZ=1 AngleXU=7.47076e-07 Radius=3.2 StartAngle=4.71239 EndAngle=6.28318
    g6: LineSegment StartX=-0.999999 StartY=-47.2 StartZ=0 EndX=-20 EndY=-47.2 EndZ=0
    g7: ArcOfCircle CenterX=-20 CenterY=-44 CenterZ=0 NormalX=0 NormalY=0 NormalZ=1 AngleXU=-1.5708 Radius=3.2 StartAngle=4.71239 EndAngle=6.28318
  constraints (12):
    c: Vertical(g0)
    c: Coincident(g0,g1)
    c: Coincident(g1,g2)
    c: Horizontal(g2)
    c: Coincident(g2,g3)
    c: Coincident(g3,g4)
    c: Vertical(g4)
    c: Coincident(g4,g5)
    c: Coincident(g5,g6)
    c: Horizontal(g6)
    c: Coincident(g6,g7)
    c: Coincident(g7,g0)
FEATURE [Sketcher::SketchObject] Sketch025  label="2.003"
  ArcFitTolerance = 1e-06
  FullyConstrained = false
  MakeInternals = false
  Placement = pos=(0,0,0) rot=(0,0,1;3.14159rad)
  sketch-geometry (8):
    g0: LineSegment StartX=-23.4 StartY=-44 StartZ=0 EndX=-23.4 EndY=-0.999999 EndZ=0
    g1: ArcOfCircle CenterX=-20 CenterY=-0.999999 CenterZ=0 NormalX=0 NormalY=0 NormalZ=1 AngleXU=0 Radius=3.4 StartAngle=1.5708 EndAngle=3.14159
    g2: LineSegment StartX=-20 StartY=2.4 StartZ=0 EndX=-0.999999 EndY=2.4 EndZ=0
    g3: ArcOfCircle CenterX=-0.999999 CenterY=-0.999999 CenterZ=0 NormalX=0 NormalY=0 NormalZ=1 AngleXU=0 Radius=3.4 StartAngle=6.28318 EndAngle=7.85398
    g4: LineSegment StartX=2.4 StartY=-1 StartZ=0 EndX=2.4 EndY=-44 EndZ=0
    g5: ArcOfCircle CenterX=-0.999999 CenterY=-44 CenterZ=0 NormalX=0 NormalY=0 NormalZ=1 AngleXU=0 Radius=3.4 StartAngle=4.71239 EndAngle=6.28318
    g6: LineSegment StartX=-0.999999 StartY=-47.4 StartZ=0 EndX=-20 EndY=-47.4 EndZ=0
    g7: ArcOfCircle CenterX=-20 CenterY=-44 CenterZ=0 NormalX=0 NormalY=0 NormalZ=1 AngleXU=0 Radius=3.4 StartAngle=3.14159 EndAngle=4.71239
  constraints (12):
    c: Vertical(g0)
    c: Coincident(g0,g1)
    c: Coincident(g1,g2)
    c: Horizontal(g2)
    c: Coincident(g2,g3)
    c: Coincident(g3,g4)
    c: Vertical(g4)
    c: Coincident(g4,g5)
    c: Coincident(g5,g6)
    c: Horizontal(g6)
    c: Coincident(g6,g7)
    c: Coincident(g7,g0)
FEATURE [PartDesign::Pad] Pad
  Direction = (0,0,1)
  Length = 3.2
  Length2 = 10
  Placement = pos=(0,0,0) rot=(0,0,1;3.14159rad)
  Profile = -> Sketch025
  ReferenceAxis = -> Sketch025 [N_Axis]
  Refine = true
  Suppressed = false
  Type = 0
FEATURE [PartDesign::Thickness] Thickness
  Base = -> Pad [Face10]
  BaseFeature = -> Pad
  Intersection = false
  Join = 0
  Mode = 0
  Refine = true
  Reversed = true
  SupportTransform = false
  Suppressed = false
  Value = 2
FEATURE [PartDesign::ShapeBinder] ShapeBinder
  Support = -> [Pcb_58ce]
  TraceSupport = false
FEATURE [Sketcher::SketchObject] Sketch026
  ArcFitTolerance = 1e-06
  AttachmentSupport = -> [Thickness]
  ExternalGeometry = -> [ShapeBinder]
  FullyConstrained = true
  MakeInternals = false
  MapMode = 5
  Placement = pos=(0,0,0) rot=(1,0,0;3.14159rad)
  sketch-geometry (4):
    g0: Circle CenterX=3 CenterY=-3 CenterZ=0 NormalX=0 NormalY=0 NormalZ=1 AngleXU=0 Radius=1.25
    g1: Circle CenterX=18 CenterY=-3 CenterZ=0 NormalX=0 NormalY=0 NormalZ=1 AngleXU=0 Radius=1.25
    g2: Circle CenterX=18 CenterY=-42 CenterZ=0 NormalX=0 NormalY=0 NormalZ=1 AngleXU=0 Radius=1.25
    g3: Circle CenterX=3 CenterY=-42 CenterZ=0 NormalX=0 NormalY=0 NormalZ=1 AngleXU=0 Radius=1.25
  constraints (8):
    c: Coincident(g0,g-3)
    c: Coincident(g1,g-4)
    c: Coincident(g2,g-5)
    c: Diameter(g2) = 2.5
    c: Equal(g0,g1)
    c: Equal(g1,g2)
    c: Coincident(g3,g-6)
    c: Equal(g2,g3)
FEATURE [PartDesign::Pocket] Pocket010
  BaseFeature = -> Thickness
  Direction = (0,0,1)
  Length = 5
  Length2 = 5
  Profile = -> Sketch026
  ReferenceAxis = -> Sketch026 [N_Axis]
  Refine = true
  Suppressed = false
  Type = 1
FEATURE [PartDesign::Chamfer] Chamfer001
  Angle = 60
  Base = -> Pocket010 [Edge18,Edge19,Edge16,Edge17]
  BaseFeature = -> Pocket010
  ChamferType = 2
  FlipDirection = false
  Refine = true
  Size = 0.8
  Size2 = 1
  SupportTransform = false
  Suppressed = false
  UseAllEdges = false
FEATURE [PartDesign::Body] Body010  label="base"
  AllowCompound = false
  Group = -> [Sketch025,Pad,Thickness,ShapeBinder,Sketch026,Pocket010,Chamfer001]
  Origin = -> Origin022
  Placement = pos=(0,0,-3.6) rot=(0,0,1;0rad)
  Tip = -> Chamfer001
FEATURE [Sketcher::SketchObject] Sketch027  label="2.004"
  ArcFitTolerance = 1e-06
  FullyConstrained = false
  MakeInternals = false
  Placement = pos=(0,0,0) rot=(0,0,1;3.14159rad)
  sketch-geometry (8):
    g0: LineSegment StartX=-23.4 StartY=-44 StartZ=0 EndX=-23.4 EndY=-1 EndZ=0
    g1: ArcOfCircle CenterX=-20 CenterY=-0.999999 CenterZ=0 NormalX=0 NormalY=0 NormalZ=1 AngleXU=0 Radius=3.4 StartAngle=1.5708 EndAngle=3.14159
    g2: LineSegment StartX=-20 StartY=2.4 StartZ=0 EndX=-1 EndY=2.4 EndZ=0
    g3: ArcOfCircle CenterX=-0.999999 CenterY=-0.999999 CenterZ=0 NormalX=0 NormalY=0 NormalZ=1 AngleXU=0 Radius=3.4 StartAngle=6.28318 EndAngle=7.85398
    g4: LineSegment StartX=2.4 StartY=-1 StartZ=0 EndX=2.4 EndY=-44 EndZ=0
    g5: ArcOfCircle CenterX=-0.999999 CenterY=-44 CenterZ=0 NormalX=0 NormalY=0 NormalZ=1 AngleXU=0 Radius=3.4 StartAngle=4.71239 EndAngle=6.28319
    g6: LineSegment StartX=-0.999999 StartY=-47.4 StartZ=0 EndX=-20 EndY=-47.4 EndZ=0
    g7: ArcOfCircle CenterX=-20 CenterY=-44 CenterZ=0 NormalX=0 NormalY=0 NormalZ=1 AngleXU=0 Radius=3.4 StartAngle=3.14159 EndAngle=4.71239
  constraints (12):
    c: Vertical(g0)
    c: Coincident(g0,g1)
    c: Coincident(g1,g2)
    c: Horizontal(g2)
    c: Coincident(g2,g3)
    c: Coincident(g3,g4)
    c: Vertical(g4)
    c: Coincident(g4,g5)
    c: Coincident(g5,g6)
    c: Horizontal(g6)
    c: Coincident(g6,g7)
    c: Coincident(g7,g0)
FEATURE [PartDesign::Pad] Pad014
  Direction = (0,0,1)
  Length = 5
  Length2 = 10
  Placement = pos=(0,0,0) rot=(0,0,1;3.14159rad)
  Profile = -> Sketch027
  ReferenceAxis = -> Sketch027 [N_Axis]
  Refine = true
  Suppressed = false
  Type = 0
FEATURE [PartDesign::Thickness] Thickness001
  Base = -> Pad014 [Face9]
  BaseFeature = -> Pad014
  Intersection = false
  Join = 0
  Mode = 0
  Refine = true
  Reversed = true
  SupportTransform = false
  Suppressed = false
  Value = 2
FEATURE [PartDesign::SubShapeBinder] Binder001
  BindCopyOnChange = 0
  BindMode = 0
  ClaimChildren = false
  Context = -> Board_58ce [Part001.Body011.Binder001.]
  Fuse = false
  MakeFace = true
  OffsetFill = false
  OffsetIntersection = false
  OffsetJoinType = 0
  OffsetOpenResult = false
  PartialLoad = false
  Refine = true
  Relative = true
  Support = -> [Step_Models_58ce[Top_58ce.S6_SKRHADE_66ce9957abdd_ln_.Part__Feature.Edge656,Top_58ce.S6_SKRHADE_66ce9957abdd_ln_.Part__Feature.Edge660,Top_58ce.SKRHADE.Part__Feature.Edge656,Top_58ce.SKRHADE.Part__Feature.Edge660]]
  _Version = 2
FEATURE [Sketcher::SketchObject] Sketch029
  ArcFitTolerance = 1e-06
  AttachmentSupport = -> [Thickness001]
  ExternalGeometry = -> [Binder001]
  FullyConstrained = false
  MakeInternals = false
  MapMode = 5
  Placement = pos=(0,0,5) rot=(0,0,1;0rad)
  sketch-geometry (6):
    g0: LineSegment [constr] StartX=11.8395 StartY=28.5203 StartZ=0 EndX=10.4199 EndY=28.5203 EndZ=0
    g1: LineSegment [constr] StartX=10.9645 StartY=27.6453 StartZ=0 EndX=10.9645 EndY=28.5203 EndZ=0
    g2: LineSegment [constr] StartX=11.8395 StartY=9.96447 StartZ=0 EndX=10.2544 EndY=9.96447 EndZ=0
    g3: LineSegment [constr] StartX=10.9645 StartY=9.08947 StartZ=0 EndX=10.9645 EndY=9.96447 EndZ=0
    g4: Circle CenterX=10.9645 CenterY=9.96447 CenterZ=0 NormalX=0 NormalY=0 NormalZ=1 AngleXU=0 Radius=4.5
    g5: Circle CenterX=10.9645 CenterY=28.5203 CenterZ=0 NormalX=0 NormalY=0 NormalZ=1 AngleXU=0 Radius=4.5
  constraints (14):
    c: Symmetric(g-4,g-4,g0)
    c: Horizontal(g0)
    c: Symmetric(g-3,g-3,g1)
    c: PointOnObject(g1,g0)
    c: Vertical(g1)
    c: Symmetric(g-6,g-6,g2)
    c: Horizontal(g2)
    c: Symmetric(g-5,g-5,g3)
    c: PointOnObject(g3,g2)
    c: Vertical(g3)
    c: Diameter(g4) = 9
    c: Coincident(g4,g3)
    c: Diameter(g5) = 9
    c: Coincident(g5,g1)
FEATURE [PartDesign::Pocket] Pocket011
  BaseFeature = -> Thickness001
  Direction = (0,0,-1)
  Length = 5
  Length2 = 5
  Profile = -> Sketch029
  ReferenceAxis = -> Sketch029 [N_Axis]
  Refine = true
  Suppressed = false
  Type = 1
FEATURE [PartDesign::SubShapeBinder] Binder002
  BindCopyOnChange = 0
  BindMode = 0
  ClaimChildren = false
  Context = -> Board_58ce [Part001.Body011.Binder002.]
  Fuse = false
  MakeFace = true
  OffsetFill = false
  OffsetIntersection = false
  OffsetJoinType = 0
  OffsetOpenResult = false
  PartialLoad = false
  Refine = true
  Relative = true
  Support = -> [Board_Geoms_58ce[Pcb_58ce.Edge35,Pcb_58ce.Edge101,Pcb_58ce.Edge134,Pcb_58ce.Edge71]]
  _Version = 2
FEATURE [Sketcher::SketchObject] Sketch030
  ArcFitTolerance = 1e-06
  AttachmentSupport = -> [Pocket011]
  ExternalGeometry = -> [Binder002]
  FullyConstrained = true
  MakeInternals = false
  MapMode = 5
  Placement = pos=(0,0,0) rot=(1,0,0;3.14159rad)
  sketch-geometry (4):
    g0: Circle CenterX=3 CenterY=-3 CenterZ=0 NormalX=0 NormalY=0 NormalZ=1 AngleXU=0 Radius=3
    g1: Circle CenterX=18 CenterY=-3 CenterZ=0 NormalX=0 NormalY=0 NormalZ=1 AngleXU=0 Radius=3
    g2: Circle CenterX=18 CenterY=-42 CenterZ=0 NormalX=0 NormalY=0 NormalZ=1 AngleXU=0 Radius=3
    g3: Circle CenterX=3 CenterY=-42 CenterZ=0 NormalX=0 NormalY=0 NormalZ=1 AngleXU=0 Radius=3
  constraints (8):
    c: Diameter(g0) = 6
    c: Coincident(g0,g-3)
    c: Diameter(g1) = 6
    c: Coincident(g1,g-4)
    c: Diameter(g2) = 6
    c: Coincident(g2,g-5)
    c: Diameter(g3) = 6
    c: Coincident(g3,g-6)
FEATURE [PartDesign::Pad] Pad015
  BaseFeature = -> Pocket011
  Direction = (0,0,-1)
  Length = 10
  Length2 = 10
  Profile = -> Sketch030
  ReferenceAxis = -> Sketch030 [N_Axis]
  Refine = true
  Suppressed = false
  Type = 3
  UpToFace = -> Pocket011 [Face21]
FEATURE [Sketcher::SketchObject] Sketch031
  ArcFitTolerance = 1e-06
  AttachmentSupport = -> [Pad015]
  ExternalGeometry = -> [Pad015]
  FullyConstrained = true
  MakeInternals = false
  MapMode = 5
  Placement = pos=(0,0,0) rot=(1,0,0;3.14159rad)
  sketch-geometry (4):
    g0: Circle CenterX=3 CenterY=-3 CenterZ=0 NormalX=0 NormalY=0 NormalZ=1 AngleXU=0 Radius=1.65
    g1: Circle CenterX=18 CenterY=-3 CenterZ=0 NormalX=0 NormalY=0 NormalZ=1 AngleXU=0 Radius=1.65
    g2: Circle CenterX=18 CenterY=-42 CenterZ=0 NormalX=0 NormalY=0 NormalZ=1 AngleXU=0 Radius=1.65
    g3: Circle CenterX=3 CenterY=-42 CenterZ=0 NormalX=0 NormalY=0 NormalZ=1 AngleXU=0 Radius=1.65
  constraints (8):
    c: Diameter(g0) = 3.3
    c: Coincident(g0,g-3)
    c: Diameter(g1) = 3.3
    c: Coincident(g1,g-4)
    c: Diameter(g2) = 3.3
    c: Coincident(g2,g-5)
    c: Diameter(g3) = 3.3
    c: Coincident(g3,g-6)
FEATURE [PartDesign::Pocket] Pocket012
  BaseFeature = -> Pad015
  Direction = (0,0,1)
  Length = 3.3
  Length2 = 5
  Profile = -> Sketch031
  ReferenceAxis = -> Sketch031 [N_Axis]
  Refine = true
  Suppressed = false
  Type = 0
FEATURE [Sketcher::SketchObject] Sketch032
  ArcFitTolerance = 1e-06
  FullyConstrained = false
  MakeInternals = false
  Placement = pos=(0,0,0) rot=(0,0,1;3.14159rad)
  sketch-geometry (8):
    g0: LineSegment StartX=-23.4 StartY=-44 StartZ=0 EndX=-23.4 EndY=-0.999999 EndZ=0
    g1: ArcOfCircle CenterX=-20 CenterY=-0.999999 CenterZ=0 NormalX=0 NormalY=0 NormalZ=1 AngleXU=-3.14159 Radius=3.4 StartAngle=4.71239 EndAngle=6.28318
    g2: LineSegment StartX=-20 StartY=2.4 StartZ=0 EndX=-0.999999 EndY=2.4 EndZ=0
    g3: ArcOfCircle CenterX=-0.999999 CenterY=-0.999999 CenterZ=0 NormalX=0 NormalY=0 NormalZ=1 AngleXU=1.5708 Radius=3.4 StartAngle=4.71239 EndAngle=6.28318
    g4: LineSegment StartX=2.4 StartY=-0.999999 StartZ=0 EndX=2.4 EndY=-44 EndZ=0
    g5: ArcOfCircle CenterX=-0.999999 CenterY=-44 CenterZ=0 NormalX=0 NormalY=0 NormalZ=1 AngleXU=7.47076e-07 Radius=3.4 StartAngle=4.71239 EndAngle=6.28318
    g6: LineSegment StartX=-0.999999 StartY=-47.4 StartZ=0 EndX=-20 EndY=-47.4 EndZ=0
    g7: ArcOfCircle CenterX=-20 CenterY=-44 CenterZ=0 NormalX=0 NormalY=0 NormalZ=1 AngleXU=-1.5708 Radius=3.4 StartAngle=4.71239 EndAngle=6.28318
  constraints (12):
    c: Vertical(g0)
    c: Coincident(g0,g1)
    c: Coincident(g1,g2)
    c: Horizontal(g2)
    c: Coincident(g2,g3)
    c: Coincident(g3,g4)
    c: Vertical(g4)
    c: Coincident(g4,g5)
    c: Coincident(g5,g6)
    c: Horizontal(g6)
    c: Coincident(g6,g7)
    c: Coincident(g7,g0)
FEATURE [Sketcher::SketchObject] Sketch033
  ArcFitTolerance = 1e-06
  AttachmentSupport = -> [Pocket012]
  ExternalGeometry = -> [Pocket012]
  FullyConstrained = false
  MakeInternals = false
  MapMode = 5
  Placement = pos=(0,47.4,0) rot=(0,0.707107,0.707107;3.14159rad)
  sketch-geometry (8):
    g0: LineSegment StartX=-14.6619 StartY=0 StartZ=0 EndX=-7.26206 EndY=0 EndZ=0
    g1: LineSegment StartX=-7.26206 StartY=0 StartZ=0 EndX=-7.26206 EndY=1.78706 EndZ=0
    g2: LineSegment StartX=-7.55642 StartY=2.08141 StartZ=0 EndX=-14.3676 EndY=2.08141 EndZ=0
    g3: LineSegment StartX=-14.6619 StartY=1.78706 StartZ=0 EndX=-14.6619 EndY=0 EndZ=0
    g4: ArcOfCircle CenterX=-14.3676 CenterY=1.78706 CenterZ=0 NormalX=0 NormalY=0 NormalZ=1 AngleXU=0 Radius=0.294356 StartAngle=1.5708 EndAngle=3.14159
    g5: GeomPoint [constr] X=-14.6619 Y=2.08141 Z=0
    g6: ArcOfCircle CenterX=-7.55642 CenterY=1.78706 CenterZ=0 NormalX=0 NormalY=0 NormalZ=1 AngleXU=0 Radius=0.294356 StartAngle=0 EndAngle=1.5708
    g7: GeomPoint [constr] X=-7.26206 Y=2.08141 Z=0
  constraints (15):
    c: Coincident(g0,g1)
    c: Coincident(g3,g0)
    c: Horizontal(g0)
    c: Horizontal(g2)
    c: Vertical(g1)
    c: Vertical(g3)
    c: PointOnObject(g0,g-3)
    c: PointOnObject(g5,g2)
    c: PointOnObject(g5,g3)
    c: Tangent(g2,g4) = -1.5708
    c: Tangent(g3,g4) = -1.5708
    c: PointOnObject(g7,g1)
    c: PointOnObject(g7,g2)
    c: Tangent(g1,g6) = -1.5708
    c: Tangent(g2,g6) = -1.5708
FEATURE [PartDesign::Pocket] Pocket
  BaseFeature = -> Pocket012
  Direction = (0,-1,2e-16)
  Length = 2
  Length2 = 5
  Profile = -> Sketch033
  ReferenceAxis = -> Sketch033 [N_Axis]
  Refine = true
  Suppressed = false
  Type = 0
FEATURE [PartDesign::Chamfer] Chamfer
  Angle = 45
  Base = -> Pocket [Edge34,Edge33]
  BaseFeature = -> Pocket
  ChamferType = 0
  FlipDirection = false
  Refine = true
  Size = 1
  Size2 = 1
  SupportTransform = false
  Suppressed = false
  UseAllEdges = false
FEATURE [PartDesign::Chamfer] Chamfer002
  Angle = 45
  Base = -> Chamfer [Edge5]
  BaseFeature = -> Chamfer
  ChamferType = 0
  FlipDirection = false
  Refine = true
  Size = 1.5
  Size2 = 1
  SupportTransform = false
  Suppressed = false
  UseAllEdges = false
FEATURE [PartDesign::Body] Body011  label="top"
  AllowCompound = false
  Group = -> [Sketch027,Pad014,Thickness001,Binder001,Sketch029,Pocket011,Binder002,Sketch030,Pad015,Sketch031,Pocket012,Sketch033,Pocket,Chamfer,Chamfer002]
  Origin = -> Origin023
  Tip = -> Chamfer002
FEATURE [App::Part] Part001  label="case"
  Group = -> [Body010,Body011]
  Origin = -> Origin021
FEATURE [App::Part] Board_58ce  label="thumb-cluster"
  Group = -> [Local_CS_58ce,Board_Geoms_58ce,Step_Models_58ce,Part001]
  Origin = -> Origin001
COMPONENT P7 — recipe-attached ("thumbstick-breakout", a linked part whose construction recipe lives in a companion FreeCAD document of the same project; that document's serialized recipe follows).
Construction recipe (the companion document, serialized — sketch geometry with constraints, then the solid features built on it; lengths are millimeters unless a unit is written):

FCSTD DOCUMENT  (FreeCAD 1.0RUnknown)
Label: thumbstick-breakout
License: All rights reserved
LicenseURL: https://en.wikipedia.org/wiki/All_rights_reserved
objects: Sketcher::SketchObject×14, App::Part×6, PartDesign::Pad×6, PartDesign::ShapeBinder×5, PartDesign::Pocket×5, PartDesign::Body×4, Part::Feature×3, PartDesign::Thickness×2, PartDesign::CoordinateSystem×1, Part::Ellipsoid×1, PartDesign::Plane×1, PartDesign::Chamfer×1, PartDesign::Revolution×1
note: 88 computed .brp shape members not serialized (recipe doc carries the construction recipe); baked Part::Feature solids carry a one-line shape summary decoded from their .brp

FEATURE [PartDesign::CoordinateSystem] Local_CS_bbd4
  AttacherType = Attacher::AttachEngine3D
  MapMode = 2
FEATURE [Part::Feature] Pcb_bbd4
  Placement = pos=(-137.3,117.78,0) rot=(0,0,1;0rad)
  shape: bbox 25.4 x 31.75 x 1.6 mm, 24 faces (baked)
FEATURE [Sketcher::SketchObject] PCB_Sketch_bbd4
  ArcFitTolerance = 1e-06
  FullyConstrained = false
  MakeInternals = false
  sketch-geometry (4):
    g0: LineSegment StartX=0 StartY=31.75 StartZ=0 EndX=0 EndY=0 EndZ=0
    g1: LineSegment StartX=25.4 StartY=31.75 StartZ=0 EndX=0 EndY=31.75 EndZ=0
    g2: LineSegment StartX=0 StartY=0 StartZ=0 EndX=25.4 EndY=0 EndZ=0
    g3: LineSegment StartX=25.4 StartY=0 StartZ=0 EndX=25.4 EndY=31.75 EndZ=0
  constraints (4):
    c: Coincident(g0,g2)
    c: Coincident(g0,g1)
    c: Coincident(g2,g3)
    c: Coincident(g1,g3)
FEATURE [App::Part] Board_Geoms_bbd4
  Group = -> [Pcb_bbd4,PCB_Sketch_bbd4]
  Origin = -> Origin
FEATURE [Part::Feature] Shape  label="J1_SOLID_4955641dfa02"
  Placement = pos=(12.66,29.4,0) rot=(0,0.707107,0.707107;3.14159rad)
  shape: bbox 4.001 x 3.601 x 0.9007 mm, 670 faces (baked)
FEATURE [App::Part] Top_bbd4
  Group = -> [Shape]
  Origin = -> Origin003
FEATURE [App::Part] Step_Models_bbd4
  Group = -> [Top_bbd4]
  Origin = -> Origin002
FEATURE [App::Part] Board_bbd4  label="thumbstick-breakout"
  Group = -> [Local_CS_bbd4,Board_Geoms_bbd4,Step_Models_bbd4]
  Origin = -> Origin001
FEATURE [Sketcher::SketchObject] Sketch009  label="2.005"
  ArcFitTolerance = 1e-06
  FullyConstrained = false
  MakeInternals = false
  sketch-geometry (8):
    g0: LineSegment StartX=-2.4 StartY=31.75 StartZ=0 EndX=-2.4 EndY=0 EndZ=0
    g1: ArcOfCircle CenterX=4.026e-13 CenterY=0 CenterZ=0 NormalX=0 NormalY=0 NormalZ=1 AngleXU=0 Radius=2.4 StartAngle=3.14159 EndAngle=4.71239
    g2: LineSegment StartX=4.70767e-08 StartY=-2.4 StartZ=0 EndX=25.4 EndY=-2.4 EndZ=0
    g3: ArcOfCircle CenterX=25.4 CenterY=0 CenterZ=0 NormalX=0 NormalY=0 NormalZ=1 AngleXU=0 Radius=2.4 StartAngle=4.71239 EndAngle=6.28318
    g4: LineSegment StartX=27.8 StartY=-7.37231e-07 StartZ=0 EndX=27.8 EndY=31.75 EndZ=0
    g5: ArcOfCircle CenterX=25.4 CenterY=31.75 CenterZ=0 NormalX=0 NormalY=0 NormalZ=1 AngleXU=0 Radius=2.4 StartAngle=0 EndAngle=1.5708
    g6: LineSegment StartX=25.4 StartY=34.15 StartZ=0 EndX=7.84308e-07 EndY=34.15 EndZ=0
    g7: ArcOfCircle CenterX=0 CenterY=31.75 CenterZ=0 NormalX=0 NormalY=0 NormalZ=1 AngleXU=0 Radius=2.4 StartAngle=1.5708 EndAngle=3.14159
  constraints (12):
    c: Vertical(g0)
    c: Coincident(g0,g1)
    c: Coincident(g1,g2)
    c: Horizontal(g2)
    c: Coincident(g2,g3)
    c: Coincident(g3,g4)
    c: Vertical(g4)
    c: Coincident(g4,g5)
    c: Coincident(g5,g6)
    c: Horizontal(g6)
    c: Coincident(g6,g7)
    c: Coincident(g7,g0)
FEATURE [PartDesign::Pad] Pad
  Direction = (0,0,1)
  Length = 3.2
  Length2 = 10
  Profile = -> Sketch009
  ReferenceAxis = -> Sketch009 [N_Axis]
  Refine = true
  Suppressed = false
  Type = 0
FEATURE [PartDesign::Thickness] Thickness001
  Base = -> Pad [Face10]
  BaseFeature = -> Pad
  Intersection = false
  Join = 0
  Mode = 0
  Refine = true
  Reversed = true
  SupportTransform = false
  Suppressed = false
  Value = 2
FEATURE [PartDesign::ShapeBinder] ShapeBinder
  Support = -> [Pcb_bbd4]
  TraceSupport = false
FEATURE [Sketcher::SketchObject] Sketch010
  ArcFitTolerance = 1e-06
  AttachmentSupport = -> [Thickness001]
  ExternalGeometry = -> [ShapeBinder]
  FullyConstrained = true
  MakeInternals = false
  MapMode = 5
  Placement = pos=(0,0,2) rot=(0,0,1;0rad)
  sketch-geometry (4):
    g0: Circle CenterX=2.54 CenterY=29.21 CenterZ=0 NormalX=0 NormalY=0 NormalZ=1 AngleXU=0 Radius=1.25
    g1: Circle CenterX=22.86 CenterY=29.21 CenterZ=0 NormalX=0 NormalY=0 NormalZ=1 AngleXU=0 Radius=1.25
    g2: Circle CenterX=22.86 CenterY=2.54 CenterZ=0 NormalX=0 NormalY=0 NormalZ=1 AngleXU=0 Radius=1.25
    g3: Circle CenterX=2.54 CenterY=2.54 CenterZ=0 NormalX=0 NormalY=0 NormalZ=1 AngleXU=0 Radius=1.25
  constraints (8):
    c: Diameter(g0) = 2.5
    c: Coincident(g0,g-3)
    c: Diameter(g1) = 2.5
    c: Coincident(g1,g-4)
    c: Diameter(g2) = 2.5
    c: Coincident(g2,g-5)
    c: Diameter(g3) = 2.5
    c: Coincident(g3,g-6)
FEATURE [PartDesign::Pocket] Pocket002
  BaseFeature = -> Thickness001
  Direction = (0,0,-1)
  Length = 5
  Length2 = 5
  Profile = -> Sketch010
  ReferenceAxis = -> Sketch010 [N_Axis]
  Refine = true
  Suppressed = false
  Type = 1
FEATURE [PartDesign::ShapeBinder] ShapeBinder003
  Support = -> [Pcb_bbd4]
  TraceSupport = false
FEATURE [Sketcher::SketchObject] Sketch011
  ArcFitTolerance = 1e-06
  AttachmentSupport = -> [Pocket002]
  ExternalGeometry = -> [ShapeBinder003]
  FullyConstrained = true
  MakeInternals = false
  MapMode = 5
  Placement = pos=(0,0,2) rot=(0,0,1;0rad)
  sketch-geometry (14):
    g0: Circle CenterX=9.45 CenterY=24.043 CenterZ=0 NormalX=0 NormalY=0 NormalZ=1 AngleXU=0 Radius=1.5
    g1: Circle CenterX=15.95 CenterY=24.043 CenterZ=0 NormalX=0 NormalY=0 NormalZ=1 AngleXU=0 Radius=1.5
    g2: Circle CenterX=15.95 CenterY=19.543 CenterZ=0 NormalX=0 NormalY=0 NormalZ=1 AngleXU=0 Radius=1.5
    g3: Circle CenterX=19.025 CenterY=18.793 CenterZ=0 NormalX=0 NormalY=0 NormalZ=1 AngleXU=0 Radius=1.5
    g4: Circle CenterX=19.025 CenterY=8.793 CenterZ=0 NormalX=0 NormalY=0 NormalZ=1 AngleXU=0 Radius=1.5
    g5: Circle CenterX=9.45 CenterY=19.543 CenterZ=0 NormalX=0 NormalY=0 NormalZ=1 AngleXU=0 Radius=1.5
    g6: Circle CenterX=6.375 CenterY=18.793 CenterZ=0 NormalX=0 NormalY=0 NormalZ=1 AngleXU=0 Radius=1.5
    g7: Circle CenterX=6.375 CenterY=8.793 CenterZ=0 NormalX=0 NormalY=0 NormalZ=1 AngleXU=0 Radius=1.5
    g8: Circle CenterX=3.97 CenterY=16.293 CenterZ=0 NormalX=0 NormalY=0 NormalZ=1 AngleXU=0 Radius=1.2
    g9: Circle CenterX=3.97 CenterY=13.793 CenterZ=0 NormalX=0 NormalY=0 NormalZ=1 AngleXU=0 Radius=1.2
    g10: Circle CenterX=3.97 CenterY=11.293 CenterZ=0 NormalX=0 NormalY=0 NormalZ=1 AngleXU=0 Radius=1.2
    g11: Circle CenterX=10.2 CenterY=5.063 CenterZ=0 NormalX=0 NormalY=0 NormalZ=1 AngleXU=0 Radius=1.2
    g12: Circle CenterX=12.7 CenterY=5.063 CenterZ=0 NormalX=0 NormalY=0 NormalZ=1 AngleXU=0 Radius=1.2
    g13: Circle CenterX=15.2 CenterY=5.063 CenterZ=0 NormalX=0 NormalY=0 NormalZ=1 AngleXU=0 Radius=1.2
  constraints (28):
    c: Diameter(g0) = 3
    c: Coincident(g0,g-3)
    c: Diameter(g1) = 3
    c: Coincident(g1,g-5)
    c: Diameter(g2) = 3
    c: Coincident(g2,g-6)
    c: Diameter(g3) = 3
    c: Coincident(g3,g-12)
    c: Diameter(g4) = 3
    c: Coincident(g4,g-13)
    c: Diameter(g5) = 3
    c: Coincident(g5,g-4)
    c: Diameter(g6) = 3
    c: Coincident(g6,g-7)
    c: Diameter(g7) = 3
    c: Coincident(g7,g-11)
    c: Diameter(g8) = 2.4
    c: Coincident(g8,g-8)
    c: Diameter(g9) = 2.4
    c: Coincident(g9,g-9)
    c: Diameter(g10) = 2.4
    c: Coincident(g10,g-10)
    c: Diameter(g11) = 2.4
    c: Coincident(g11,g-16)
    c: Diameter(g12) = 2.4
    c: Coincident(g12,g-15)
    c: Diameter(g13) = 2.4
    c: Coincident(g13,g-14)
FEATURE [PartDesign::Pocket] Pocket003
  BaseFeature = -> Pocket002
  Direction = (0,0,-1)
  Length = 1
  Length2 = 5
  Profile = -> Sketch011
  ReferenceAxis = -> Sketch011 [N_Axis]
  Refine = true
  Suppressed = false
  Type = 0
FEATURE [PartDesign::Body] Body  label="base"
  AllowCompound = false
  Group = -> [Sketch009,Pad,Thickness001,ShapeBinder,Sketch010,Pocket002,ShapeBinder003,Sketch011,Pocket003]
  Origin = -> Origin010
  Placement = pos=(0,0,-3.6) rot=(0,0,1;0rad)
  Tip = -> Pocket003
FEATURE [PartDesign::ShapeBinder] ShapeBinder004
  Placement = pos=(-137.3,117.78,0) rot=(0,0,1;0rad)
  Support = -> [Pcb_bbd4]
  TraceSupport = false
FEATURE [Sketcher::SketchObject] Sketch012
  ArcFitTolerance = 1e-06
  AttachmentSupport = -> [ShapeBinder004]
  ExternalGeometry = -> [ShapeBinder004]
  FullyConstrained = false
  MakeInternals = false
  MapMode = 5
  Placement = pos=(-137.3,117.78,0) rot=(0,0,1;0rad)
  sketch-geometry (15):
    g0: Circle CenterX=146.75 CenterY=-93.737 CenterZ=0 NormalX=0 NormalY=0 NormalZ=1 AngleXU=0 Radius=0.2
    g1: Circle CenterX=153.25 CenterY=-93.737 CenterZ=0 NormalX=0 NormalY=0 NormalZ=1 AngleXU=0 Radius=0.2
    g2: Circle CenterX=153.25 CenterY=-98.237 CenterZ=0 NormalX=0 NormalY=0 NormalZ=1 AngleXU=0 Radius=0.2
    g3: Circle CenterX=156.325 CenterY=-98.987 CenterZ=0 NormalX=0 NormalY=0 NormalZ=1 AngleXU=0 Radius=0.2
    g4: Circle CenterX=146.75 CenterY=-98.237 CenterZ=0 NormalX=0 NormalY=0 NormalZ=1 AngleXU=0 Radius=0.2
    g5: Circle CenterX=143.675 CenterY=-98.987 CenterZ=0 NormalX=0 NormalY=0 NormalZ=1 AngleXU=0 Radius=0.2
    g6: Circle CenterX=141.27 CenterY=-101.487 CenterZ=0 NormalX=0 NormalY=0 NormalZ=1 AngleXU=0 Radius=0.2
    g7: Circle CenterX=141.27 CenterY=-103.987 CenterZ=0 NormalX=0 NormalY=0 NormalZ=1 AngleXU=0 Radius=0.2
    g8: Circle CenterX=141.27 CenterY=-106.487 CenterZ=0 NormalX=0 NormalY=0 NormalZ=1 AngleXU=0 Radius=0.2
    g9: Circle CenterX=143.675 CenterY=-108.987 CenterZ=0 NormalX=0 NormalY=0 NormalZ=1 AngleXU=0 Radius=0.2
    g10: Circle CenterX=147.5 CenterY=-112.717 CenterZ=0 NormalX=0 NormalY=0 NormalZ=1 AngleXU=0 Radius=0.2
    g11: Circle CenterX=150 CenterY=-112.717 CenterZ=0 NormalX=0 NormalY=0 NormalZ=1 AngleXU=0 Radius=0.2
    g12: Circle CenterX=152.5 CenterY=-112.717 CenterZ=0 NormalX=0 NormalY=0 NormalZ=1 AngleXU=0 Radius=0.2
    g13: Circle CenterX=152.599 CenterY=-112.925 CenterZ=0 NormalX=0 NormalY=0 NormalZ=1 AngleXU=0 Radius=0.2
    g14: Circle CenterX=156.325 CenterY=-108.987 CenterZ=0 NormalX=0 NormalY=0 NormalZ=1 AngleXU=0 Radius=0.2
  constraints (15):
    c: Coincident(g0,g-3)
    c: Coincident(g1,g-4)
    c: Coincident(g2,g-5)
    c: Coincident(g3,g-6)
    c: Coincident(g4,g-7)
    c: Coincident(g5,g-8)
    c: Coincident(g6,g-9)
    c: Coincident(g7,g-10)
    c: Coincident(g8,g-11)
    c: Coincident(g9,g-12)
    c: Coincident(g10,g-13)
    c: Coincident(g11,g-14)
    c: Coincident(g14,g-16)
    c: Equal(g0, g1-g14) x14
    c: Radius(g0) = 0.2
FEATURE [Sketcher::SketchObject] Sketch013
  ArcFitTolerance = 1e-06
  AttachmentSupport = -> [XY_Plane012]
  ExternalGeometry = -> [ShapeBinder004]
  FullyConstrained = false
  MakeInternals = false
  MapMode = 5
  sketch-geometry (14):
    g0: LineSegment StartX=17.3886 StartY=25.1014 StartZ=0 EndX=8.04245 EndY=25.1014 EndZ=0
    g1: LineSegment StartX=6.375 StartY=18.793 StartZ=0 EndX=2.6831 EndY=18.793 EndZ=0
    g2: LineSegment StartX=2.6831 StartY=18.793 StartZ=0 EndX=2.6831 EndY=8.793 EndZ=0
    g3: LineSegment StartX=2.6831 StartY=8.793 StartZ=0 EndX=6.375 EndY=8.793 EndZ=0
    g4: LineSegment StartX=8.26567 StartY=4.26908 StartZ=0 EndX=16.6861 EndY=4.26908 EndZ=0
    g5: LineSegment StartX=16.6861 StartY=4.26908 StartZ=0 EndX=16.6861 EndY=8.793 EndZ=0
    g6: LineSegment StartX=16.6861 StartY=8.793 StartZ=0 EndX=19.025 EndY=8.793 EndZ=0
    g7: LineSegment StartX=19.025 StartY=8.793 StartZ=0 EndX=19.025 EndY=18.793 EndZ=0
    g8: LineSegment StartX=19.025 StartY=18.793 StartZ=0 EndX=17.3886 EndY=18.793 EndZ=0
    g9: LineSegment StartX=17.3886 StartY=18.793 StartZ=0 EndX=17.3886 EndY=25.1014 EndZ=0
    g10: LineSegment StartX=6.375 StartY=18.793 StartZ=0 EndX=8.04245 EndY=18.793 EndZ=0
    g11: LineSegment StartX=8.04245 StartY=18.793 StartZ=0 EndX=8.04245 EndY=25.1014 EndZ=0
    g12: LineSegment StartX=6.375 StartY=8.793 StartZ=0 EndX=8.26567 EndY=8.793 EndZ=0
    g13: LineSegment StartX=8.26567 StartY=8.793 StartZ=0 EndX=8.26567 EndY=4.26908 EndZ=0
  constraints (30):
    c: Horizontal(g0)
    c: Horizontal(g1)
    c: Coincident(g1,g2)
    c: Vertical(g2)
    c: Coincident(g2,g3)
    c: Horizontal(g3)
    c: Horizontal(g4)
    c: Coincident(g4,g5)
    c: Vertical(g5)
    c: Coincident(g5,g6)
    c: Horizontal(g6)
    c: Coincident(g6,g7)
    c: Coincident(g7,g8)
    c: Horizontal(g8)
    c: Coincident(g8,g9)
    c: Coincident(g9,g0)
    c: Vertical(g9)
    c: Coincident(g7,g-8)
    c: Coincident(g6,g-9)
    c: Coincident(g3,g-10)
    c: Coincident(g1,g10)
    c: Horizontal(g10)
    c: Coincident(g10,g11)
    c: Coincident(g11,g0)
    c: Vertical(g11)
    c: Coincident(g3,g12)
    c: Horizontal(g12)
    c: Coincident(g12,g13)
    c: Coincident(g13,g4)
    c: Vertical(g13)
FEATURE [PartDesign::Pad] Pad001
  Direction = (0,0,1)
  Length = 9.3
  Length2 = 10
  Profile = -> Sketch013
  ReferenceAxis = -> Sketch013 [N_Axis]
  Refine = true
  Suppressed = false
  Type = 0
FEATURE [PartDesign::Pad] Pad002
  BaseFeature = -> Pad001
  Direction = (0,0,1)
  Length = 2
  Length2 = 10
  Profile = -> Sketch012
  ReferenceAxis = -> Sketch012 [N_Axis]
  Refine = true
  Reversed = true
  Suppressed = false
  Type = 0
FEATURE [PartDesign::Body] Body001  label="Body"
  AllowCompound = false
  Group = -> [ShapeBinder004,Sketch012,Sketch013,Pad001,Pad002]
  Origin = -> Origin012
  Tip = -> Pad002
FEATURE [Sketcher::SketchObject] Sketch014  label="2.4"
  ArcFitTolerance = 1e-06
  FullyConstrained = false
  MakeInternals = false
  sketch-geometry (8):
    g0: LineSegment StartX=-2.4 StartY=31.75 StartZ=0 EndX=-2.4 EndY=0 EndZ=0
    g1: ArcOfCircle CenterX=0 CenterY=0 CenterZ=0 NormalX=0 NormalY=0 NormalZ=1 AngleXU=0 Radius=2.4 StartAngle=3.14159 EndAngle=4.71239
    g2: LineSegment StartX=-4e-16 StartY=-2.4 StartZ=0 EndX=25.4 EndY=-2.4 EndZ=0
    g3: ArcOfCircle CenterX=25.4 CenterY=0 CenterZ=0 NormalX=0 NormalY=0 NormalZ=1 AngleXU=1.5708 Radius=2.4 StartAngle=3.14159 EndAngle=4.71239
    g4: LineSegment StartX=27.8 StartY=-4e-16 StartZ=0 EndX=27.8 EndY=31.75 EndZ=0
    g5: ArcOfCircle CenterX=25.4 CenterY=31.75 CenterZ=0 NormalX=0 NormalY=0 NormalZ=1 AngleXU=-3.14159 Radius=2.4 StartAngle=3.14159 EndAngle=4.71239
    g6: LineSegment StartX=25.4 StartY=34.15 StartZ=0 EndX=0 EndY=34.15 EndZ=0
    g7: ArcOfCircle CenterX=0 CenterY=31.75 CenterZ=0 NormalX=0 NormalY=0 NormalZ=1 AngleXU=-1.5708 Radius=2.4 StartAngle=3.14159 EndAngle=4.71239
  constraints (12):
    c: Vertical(g0)
    c: Coincident(g0,g1)
    c: Coincident(g1,g2)
    c: Horizontal(g2)
    c: Coincident(g2,g3)
    c: Coincident(g3,g4)
    c: Vertical(g4)
    c: Coincident(g4,g5)
    c: Coincident(g5,g6)
    c: Horizontal(g6)
    c: Coincident(g6,g7)
    c: Coincident(g7,g0)
FEATURE [PartDesign::ShapeBinder] ShapeBinder005
  Support = -> [Pcb_bbd4]
  TraceSupport = false
FEATURE [Sketcher::SketchObject] Sketch
  ArcFitTolerance = 1e-06
  AttachmentSupport = -> [XY_Plane013]
  ExternalGeometry = -> [ShapeBinder005]
  FullyConstrained = true
  MakeInternals = false
  MapMode = 5
  sketch-geometry (2):
    g0: LineSegment [constr] StartX=6.375 StartY=18.793 StartZ=0 EndX=19.025 EndY=8.793 EndZ=0
    g1: Circle CenterX=12.7 CenterY=13.793 CenterZ=0 NormalX=0 NormalY=0 NormalZ=1 AngleXU=0 Radius=2
  constraints (4):
    c: Coincident(g0,g-3)
    c: Coincident(g0,g-5)
    c: Symmetric(g0,g0,g1)
    c: Diameter(g1) = 4
FEATURE [PartDesign::Pad] Pad003
  Direction = (0,0,1)
  Length = 12
  Length2 = 10
  Profile = -> Sketch
  ReferenceAxis = -> Sketch [N_Axis]
  Refine = true
  Suppressed = false
  Type = 0
FEATURE [PartDesign::Body] Body002  label="stick"
  AllowCompound = false
  Group = -> [ShapeBinder005,Sketch,Pad003]
  Origin = -> Origin013
  Placement = pos=(0,0,6.5) rot=(0,0,1;0rad)
  Tip = -> Pad003
FEATURE [Part::Feature] Part__Feature001  label="Thumbstick"
  Placement = pos=(12.7,13.8,-2.8) rot=(0,0,1;0rad)
  shape: bbox 24.74 x 24.74 x 17.5 mm, 20 faces (baked)
FEATURE [App::Part] Part  label="thumbstick"
  Group = -> [Body001,Body002,Part__Feature001]
  Origin = -> Origin011
FEATURE [Sketcher::SketchObject] Sketch015  label="2.006"
  ArcFitTolerance = 1e-06
  FullyConstrained = false
  MakeInternals = false
  sketch-geometry (8):
    g0: LineSegment StartX=-2.4 StartY=31.75 StartZ=0 EndX=-2.4 EndY=0 EndZ=0
    g1: ArcOfCircle CenterX=0 CenterY=0 CenterZ=0 NormalX=0 NormalY=0 NormalZ=1 AngleXU=0 Radius=2.4 StartAngle=3.14159 EndAngle=4.71239
    g2: LineSegment StartX=-4e-16 StartY=-2.4 StartZ=0 EndX=25.4 EndY=-2.4 EndZ=0
    g3: ArcOfCircle CenterX=25.4 CenterY=0 CenterZ=0 NormalX=0 NormalY=0 NormalZ=1 AngleXU=1.5708 Radius=2.4 StartAngle=3.14159 EndAngle=4.71239
    g4: LineSegment StartX=27.8 StartY=-7e-16 StartZ=0 EndX=27.8 EndY=31.75 EndZ=0
    g5: ArcOfCircle CenterX=25.4 CenterY=31.75 CenterZ=0 NormalX=0 NormalY=0 NormalZ=1 AngleXU=-3.14159 Radius=2.4 StartAngle=3.14159 EndAngle=4.71239
    g6: LineSegment StartX=25.4 StartY=34.15 StartZ=0 EndX=0 EndY=34.15 EndZ=0
    g7: ArcOfCircle CenterX=0 CenterY=31.75 CenterZ=0 NormalX=0 NormalY=0 NormalZ=1 AngleXU=-1.5708 Radius=2.4 StartAngle=3.14159 EndAngle=4.71239
  constraints (12):
    c: Vertical(g0)
    c: Coincident(g0,g1)
    c: Coincident(g1,g2)
    c: Horizontal(g2)
    c: Coincident(g2,g3)
    c: Coincident(g3,g4)
    c: Vertical(g4)
    c: Coincident(g4,g5)
    c: Coincident(g5,g6)
    c: Horizontal(g6)
    c: Coincident(g6,g7)
    c: Coincident(g7,g0)
FEATURE [PartDesign::Pad] Pad004
  Direction = (0,0,1)
  Length = 5.3
  Length2 = 10
  Profile = -> Sketch015
  ReferenceAxis = -> Sketch015 [N_Axis]
  Refine = true
  Suppressed = false
  Type = 0
FEATURE [PartDesign::Thickness] Thickness
  Base = -> Pad004 [Face9]
  BaseFeature = -> Pad004
  Intersection = false
  Join = 0
  Mode = 0
  Refine = true
  Reversed = true
  SupportTransform = false
  Suppressed = false
  Value = 2
FEATURE [PartDesign::ShapeBinder] ShapeBinder006
  Support = -> [Pocket003]
  TraceSupport = false
FEATURE [Sketcher::SketchObject] Sketch016
  ArcFitTolerance = 1e-06
  AttachmentSupport = -> [Thickness]
  ExternalGeometry = -> [ShapeBinder006]
  FullyConstrained = true
  MakeInternals = false
  MapMode = 5
  Placement = pos=(0,0,0) rot=(1,0,0;3.14159rad)
  sketch-geometry (8):
    g0: Circle CenterX=2.54 CenterY=-2.54 CenterZ=0 NormalX=0 NormalY=0 NormalZ=1 AngleXU=0 Radius=3
    g1: Circle CenterX=22.86 CenterY=-2.54 CenterZ=0 NormalX=0 NormalY=0 NormalZ=1 AngleXU=0 Radius=3
    g2: Circle CenterX=22.86 CenterY=-29.21 CenterZ=0 NormalX=0 NormalY=0 NormalZ=1 AngleXU=0 Radius=3
    g3: Circle CenterX=2.54 CenterY=-29.21 CenterZ=0 NormalX=0 NormalY=0 NormalZ=1 AngleXU=0 Radius=3
    g4: Circle CenterX=2.54 CenterY=-2.54 CenterZ=0 NormalX=0 NormalY=0 NormalZ=1 AngleXU=0 Radius=1.65
    g5: Circle CenterX=22.86 CenterY=-2.54 CenterZ=0 NormalX=0 NormalY=0 NormalZ=1 AngleXU=0 Radius=1.65
    g6: Circle CenterX=22.86 CenterY=-29.21 CenterZ=0 NormalX=0 NormalY=0 NormalZ=1 AngleXU=0 Radius=1.65
    g7: Circle CenterX=2.54 CenterY=-29.21 CenterZ=0 NormalX=0 NormalY=0 NormalZ=1 AngleXU=0 Radius=1.65
  constraints (16):
    c: Diameter(g0) = 6
    c: Coincident(g0,g-3)
    c: Diameter(g1) = 6
    c: Coincident(g1,g-4)
    c: Diameter(g2) = 6
    c: Coincident(g2,g-5)
    c: Diameter(g3) = 6
    c: Coincident(g3,g-6)
    c: Diameter(g4) = 3.3
    c: Coincident(g4,g0)
    c: Diameter(g5) = 3.3
    c: Coincident(g5,g1)
    c: Diameter(g6) = 3.3
    c: Coincident(g6,g2)
    c: Diameter(g7) = 3.3
    c: Coincident(g7,g3)
FEATURE [Part::Ellipsoid] Ellipsoid
  Angle1 = -90
  Angle2 = 90
  Angle3 = 180
  AttacherType = Attacher::AttachEngine3D
  Placement = pos=(12.7,13.8,9.3) rot=(1,0,0;1.5708rad)
  Radius1 = 12.37
  Radius2 = 12.37
  Radius3 = 8
FEATURE [PartDesign::Plane] DatumPlane
  AttachmentOffset = pos=(0,0,12.7) rot=(0,0,1;0rad)
  AttachmentSupport = -> [YZ_Plane014]
  Length = 70.0266
  MapMode = 5
  Placement = pos=(12.7,0,0) rot=(0.57735,0.57735,0.57735;2.0944rad)
  ResizeMode = 0
  Width = 60.8766
FEATURE [Sketcher::SketchObject] Sketch017
  ArcFitTolerance = 1e-06
  AttachmentSupport = -> [DatumPlane]
  FullyConstrained = false
  MakeInternals = false
  MapMode = 5
  Placement = pos=(12.7,0,0) rot=(0.57735,0.57735,0.57735;2.0944rad)
  sketch-geometry (18):
    g0: Circle [constr] CenterX=29.1118 CenterY=3.8 CenterZ=0 NormalX=0 NormalY=0 NormalZ=1 AngleXU=0 Radius=1
    g1: Circle [constr] CenterX=30.0485 CenterY=13.7535 CenterZ=0 NormalX=0 NormalY=0 NormalZ=1 AngleXU=0 Radius=1
    g2: Circle [constr] CenterX=23.3909 CenterY=17.1877 CenterZ=0 NormalX=0 NormalY=0 NormalZ=1 AngleXU=0 Radius=1
    g3: BSplineCurve PolesCount=3 KnotsCount=2 Degree=2 IsPeriodic=0
    g4: GeomPoint [constr] X=29.1118 Y=3.8 Z=0
    g5: GeomPoint [constr] X=23.3909 Y=17.1877 Z=0
    g6: LineSegment StartX=23.3909 StartY=17.1877 StartZ=0 EndX=13.7824 EndY=17.1877 EndZ=0
    g7: Circle [constr] CenterX=28.1118 CenterY=3.8 CenterZ=0 NormalX=0 NormalY=0 NormalZ=1 AngleXU=0 Radius=1
    g8: Circle [constr] CenterX=28.4002 CenterY=12.6207 CenterZ=0 NormalX=0 NormalY=0 NormalZ=1 AngleXU=0 Radius=1
    g9: Circle [constr] CenterX=23.1917 CenterY=16.2077 CenterZ=0 NormalX=0 NormalY=0 NormalZ=1 AngleXU=0 Radius=1
    g10: BSplineCurve PolesCount=3 KnotsCount=2 Degree=2 IsPeriodic=0
    g11: GeomPoint [constr] X=28.1118 Y=3.8 Z=0
    g12: GeomPoint [constr] X=23.1917 Y=16.2077 Z=0
    g13: LineSegment StartX=28.1118 StartY=3.8 StartZ=0 EndX=29.1118 EndY=3.8 EndZ=0
    g14: LineSegment StartX=13.7824 StartY=17.1877 StartZ=0 EndX=13.7824 EndY=16.2077 EndZ=0
    g15: LineSegment StartX=13.7824 StartY=16.2077 StartZ=0 EndX=23.1917 EndY=16.2077 EndZ=0
    g16: LineSegment [constr] StartX=1.40969 StartY=9.23031 StartZ=0 EndX=26.155 EndY=9.23031 EndZ=0
    g17: LineSegment [constr] StartX=13.7824 StartY=9.23031 StartZ=0 EndX=13.7824 EndY=17.9973 EndZ=0
  constraints (33):
    c: Weight(g0) = 1
    c: Equal(g0,g1)
    c: Equal(g0,g2)
    c: InternalAlignment(g0,g3)
    c: InternalAlignment(g1,g3)
    c: InternalAlignment(g2,g3)
    c: InternalAlignment(g4,g3)
    c: InternalAlignment(g5,g3)
    c: Coincident(g6,g3)
    c: Horizontal(g6)
    c: Weight(g7) = 1
    c: Equal(g7,g8)
    c: Equal(g7,g9)
    c: InternalAlignment(g7,g10)
    c: InternalAlignment(g8,g10)
    c: InternalAlignment(g9,g10)
    c: InternalAlignment(g11,g10)
    c: InternalAlignment(g12,g10)
    c: Coincident(g13,g10)
    c: Coincident(g13,g3)
    c: Horizontal(g13)
    c: DistanceX(g13,g13) = 1
    c: Distance(g3,g10) = 1
    c: Distance(g1,g8) = 2
    c: Coincident(g6,g14)
    c: Vertical(g14)
    c: Coincident(g15,g10)
    c: Horizontal(g15)
    c: Horizontal(g16)
    c: Symmetric(g16,g16,g17)
    c: Vertical(g17)
    c: PointOnObject(g6,g17)
    c: Distance(g10,g-3) = 1.5
FEATURE [PartDesign::Chamfer] Chamfer
  Angle = 45
  Base = -> Thickness [Edge4]
  BaseFeature = -> Thickness
  ChamferType = 0
  FlipDirection = false
  Refine = true
  Size = 1.5
  Size2 = 1
  SupportTransform = false
  Suppressed = false
  UseAllEdges = false
FEATURE [PartDesign::Pad] Pad005
  BaseFeature = -> Chamfer
  Direction = (0,0,-1)
  Length = 3.3
  Length2 = 10
  Profile = -> Sketch016
  ReferenceAxis = -> Sketch016 [N_Axis]
  Refine = true
  Reversed = true
  Suppressed = false
  Type = 0
FEATURE [PartDesign::Revolution] Revolution
  Angle = 360
  Angle2 = 60
  Axis = (0,0,-1)
  Base = (12.7,13.7824,17.1877)
  BaseFeature = -> Pad005
  Profile = -> Sketch017
  ReferenceAxis = -> Sketch017 [Edge4]
  Refine = true
  Reversed = true
  Suppressed = false
  Type = 0
FEATURE [Sketcher::SketchObject] Sketch018
  ArcFitTolerance = 1e-06
  AttachmentSupport = -> [Revolution]
  ExternalGeometry = -> [Revolution]
  FullyConstrained = true
  MakeInternals = false
  MapMode = 5
  Placement = pos=(0,0,17.1877) rot=(0,0,1;0rad)
  sketch-geometry (1):
    g0: Circle CenterX=12.7 CenterY=13.7824 CenterZ=0 NormalX=0 NormalY=0 NormalZ=1 AngleXU=0 Radius=9.5
  constraints (2):
    c: Coincident(g0,g-3)
    c: Diameter(g0) = 19
FEATURE [PartDesign::Pocket] Pocket
  BaseFeature = -> Revolution
  Direction = (0,0,-1)
  Length = 14
  Length2 = 5
  Profile = -> Sketch018
  ReferenceAxis = -> Sketch018 [N_Axis]
  Refine = true
  Suppressed = false
  Type = 0
FEATURE [Sketcher::SketchObject] Sketch019
  ArcFitTolerance = 1e-06
  AttachmentSupport = -> [Pocket]
  FullyConstrained = true
  MakeInternals = false
  MapMode = 5
  Placement = pos=(0,0,5.3) rot=(0,0,1;0rad)
  sketch-geometry (1):
    g0: Circle CenterX=12.7 CenterY=13.7824 CenterZ=0 NormalX=0 NormalY=0 NormalZ=1 AngleXU=0 Radius=14.157
  constraints (2):
    c: Coincident(g0,g-3)
    c: Equal(g0,g-3)
FEATURE [PartDesign::Pocket] Pocket004
  BaseFeature = -> Pocket
  Direction = (0,0,-1)
  Length = 2
  Length2 = 5
  Profile = -> Sketch019
  ReferenceAxis = -> Sketch019 [N_Axis]
  Refine = true
  Suppressed = false
  Type = 0
FEATURE [Sketcher::SketchObject] Sketch020
  ArcFitTolerance = 1e-06
  AttachmentSupport = -> [Pocket004]
  ExternalGeometry = -> [Pocket004]
  FullyConstrained = false
  MakeInternals = false
  MapMode = 5
  Placement = pos=(0,34.15,0) rot=(0,0.707107,0.707107;3.14159rad)
  sketch-geometry (4):
    g0: LineSegment StartX=-15.1629 StartY=0 StartZ=0 EndX=-10.1629 EndY=0 EndZ=0
    g1: LineSegment StartX=-10.1629 StartY=0 StartZ=0 EndX=-10.1629 EndY=1.3 EndZ=0
    g2: LineSegment StartX=-10.1629 StartY=1.3 StartZ=0 EndX=-15.1629 EndY=1.3 EndZ=0
    g3: LineSegment StartX=-15.1629 StartY=1.3 StartZ=0 EndX=-15.1629 EndY=0 EndZ=0
  constraints (11):
    c: Coincident(g0,g1)
    c: Coincident(g1,g2)
    c: Coincident(g2,g3)
    c: Coincident(g3,g0)
    c: Horizontal(g0)
    c: Horizontal(g2)
    c: Vertical(g1)
    c: Vertical(g3)
    c: PointOnObject(g0,g-3)
    c: DistanceX(g2,g2) = 5
    c: DistanceY(g1,g1) = 1.3
FEATURE [PartDesign::Pocket] Pocket005
  BaseFeature = -> Pocket004
  Direction = (0,-1,2e-16)
  Length = 2
  Length2 = 5
  Profile = -> Sketch020
  ReferenceAxis = -> Sketch020 [N_Axis]
  Refine = true
  Suppressed = false
  Type = 0
FEATURE [PartDesign::Body] Body003  label="top"
  AllowCompound = false
  Group = -> [Sketch015,Pad004,Thickness,Chamfer,ShapeBinder006,Sketch016,Pad005,DatumPlane,Sketch017,Revolution,Sketch018,Pocket,Sketch019,Pocket004,Sketch020,Pocket005]
  Origin = -> Origin014
  Tip = -> Pocket005
FEATURE [App::Part] Part001  label="case"
  Group = -> [Body,Body003,Ellipsoid]
  Origin = -> Origin009
COMPONENT P8 — recipe-attached ("xring", modeled in this document).
Construction recipe (the document's own serialized feature program — sketch geometry with constraints, then the solid features built on it; lengths are millimeters unless a unit is written):

FEATURE [Sketcher::SketchObject] PCB_Sketch_f9e4  label="left"
  ArcFitTolerance = 1e-06
  FullyConstrained = false
  MakeInternals = false
  MapMode = 5
  Placement = pos=(0,0,0) rot=(0,-1,0;1.5708rad)
  sketch-geometry (21):
    g0: LineSegment StartX=48.9342 StartY=15.25 StartZ=0 EndX=77.5946 EndY=15.25 EndZ=0
    g1: LineSegment StartX=27.2503 StartY=38.2054 StartZ=0 EndX=0.583058 EndY=26.0175 EndZ=0
    g2: LineSegment StartX=126 StartY=8.65 StartZ=0 EndX=126 EndY=45.95 EndZ=0
    g3: LineSegment StartX=9e-16 StartY=25.1085 StartZ=0 EndX=0 EndY=1 EndZ=0
    g4: LineSegment StartX=104.439 StartY=47.8424 StartZ=0 EndX=27.5489 EndY=38.289 EndZ=0
    g5: LineSegment StartX=34.5465 StartY=0.317255 StartZ=0 EndX=48.2035 EndY=14.9327 EndZ=0
    g6: LineSegment StartX=104.562 StartY=47.85 StartZ=0 EndX=125 EndY=47.85 EndZ=0
    g7: LineSegment StartX=125 StartY=7.65 StartZ=0 EndX=88.6266 EndY=7.65 EndZ=0
    g8: LineSegment StartX=1 StartY=1e-16 StartZ=0 EndX=33.8158 EndY=-1.6e-15 EndZ=0
    g9: LineSegment StartX=126 StartY=45.95 StartZ=0 EndX=126 EndY=46.85 EndZ=0
    g10: LineSegment StartX=78.291 StartY=14.9676 StartZ=0 EndX=88.0364 EndY=7.84274 EndZ=0
    g11: ArcOfCircle CenterX=27.666 CenterY=37.2959 CenterZ=0 NormalX=0 NormalY=0 NormalZ=-1 AngleXU=1.14211 Radius=1.00001 StartAngle=0 EndAngle=0.311303
    g12: ArcOfCircle CenterX=33.8158 CenterY=1.00002 CenterZ=0 NormalX=0 NormalY=0 NormalZ=-1 AngleXU=-2.39007 Radius=1.00002 StartAngle=0 EndAngle=0.81927
    g13: ArcOfCircle CenterX=48.9342 CenterY=14.25 CenterZ=0 NormalX=0 NormalY=0 NormalZ=-1 AngleXU=0.75152 Radius=1.00002 StartAngle=0 EndAngle=0.81927
    g14: ArcOfCircle CenterX=125 CenterY=46.85 CenterZ=0 NormalX=0 NormalY=0 NormalZ=-1 AngleXU=1.5708 Radius=0.999999 StartAngle=0 EndAngle=1.5708
    g15: ArcOfCircle CenterX=125 CenterY=8.65 CenterZ=0 NormalX=0 NormalY=0 NormalZ=-1 AngleXU=3.14159 Radius=0.999999 StartAngle=0 EndAngle=1.5708
    g16: ArcOfCircle CenterX=88.6266 CenterY=8.65 CenterZ=0 NormalX=0 NormalY=0 NormalZ=-1 AngleXU=-1.57079 Radius=1 StartAngle=0 EndAngle=0.631296
    g17: ArcOfCircle CenterX=104.562 CenterY=46.8498 CenterZ=0 NormalX=0 NormalY=0 NormalZ=-1 AngleXU=1.44719 Radius=1.00016 StartAngle=0 EndAngle=0.123594
    g18: ArcOfCircle CenterX=0.999999 CenterY=0.999999 CenterZ=0 NormalX=0 NormalY=0 NormalZ=-1 AngleXU=-1.5708 Radius=0.999999 StartAngle=0 EndAngle=1.5708
    g19: ArcOfCircle CenterX=1.00007 CenterY=25.1085 CenterZ=0 NormalX=0 NormalY=0 NormalZ=-1 AngleXU=4.52044e-05 Radius=1.00007 StartAngle=0 EndAngle=1.14063
    g20: ArcOfCircle CenterX=77.5946 CenterY=14.25 CenterZ=0 NormalX=0 NormalY=0 NormalZ=-1 AngleXU=1.57078 Radius=0.999961 StartAngle=0 EndAngle=0.770416
  constraints (21):
    c: Coincident(g3,g18)
    c: Coincident(g3,g19)
    c: Coincident(g1,g19)
    c: Coincident(g8,g18)
    c: Coincident(g1,g11)
    c: Coincident(g4,g11)
    c: Coincident(g8,g12)
    c: Coincident(g5,g12)
    c: Coincident(g5,g13)
    c: Coincident(g0,g13)
    c: Coincident(g0,g20)
    c: Coincident(g10,g20)
    c: Coincident(g10,g16)
    c: Coincident(g7,g16)
    c: Coincident(g4,g17)
    c: Coincident(g6,g17)
    c: Coincident(g7,g15)
    c: Coincident(g6,g14)
    c: Coincident(g2,g15)
    c: Coincident(g2,g9)
    c: Coincident(g9,g14)
FEATURE [PartDesign::Pad] Pad
  Direction = (-1,0,2e-16)
  Length = 2
  Length2 = 10
  Placement = pos=(0,0,0) rot=(0,-1,0;1.5708rad)
  Profile = -> PCB_Sketch_f9e4
  ReferenceAxis = -> PCB_Sketch_f9e4 [N_Axis]
  Refine = true
  Suppressed = false
  Type = 0
FEATURE [Sketcher::SketchObject] PCB_Sketch_f9e005  label="left holes"
  ArcFitTolerance = 1e-06
  AttachmentSupport = -> [Pad]
  FullyConstrained = false
  MakeInternals = false
  MapMode = 5
  Placement = pos=(-2,0,4e-16) rot=(0,-1,0;1.5708rad)
  sketch-geometry (8):
    g0: Circle CenterX=4.15 CenterY=23.1667 CenterZ=0 NormalX=0 NormalY=0 NormalZ=1 AngleXU=0 Radius=3
    g1: Circle CenterX=4.15 CenterY=4.65 CenterZ=0 NormalX=0 NormalY=0 NormalZ=1 AngleXU=0 Radius=3
    g2: Circle CenterX=95.5 CenterY=43.35 CenterZ=0 NormalX=0 NormalY=0 NormalZ=1 AngleXU=0 Radius=3
    g3: Circle CenterX=99.8333 CenterY=10.6833 CenterZ=0 NormalX=0 NormalY=0 NormalZ=1 AngleXU=0 Radius=3
    g4: Circle CenterX=95.5 CenterY=43.35 CenterZ=0 NormalX=0 NormalY=0 NormalZ=1 AngleXU=0 Radius=1.65
    g5: Circle CenterX=99.8333 CenterY=10.6833 CenterZ=0 NormalX=0 NormalY=0 NormalZ=1 AngleXU=0 Radius=1.65
    g6: Circle CenterX=4.15 CenterY=23.1667 CenterZ=0 NormalX=0 NormalY=0 NormalZ=1 AngleXU=0 Radius=1.65
    g7: Circle CenterX=4.15 CenterY=4.65 CenterZ=0 NormalX=0 NormalY=0 NormalZ=1 AngleXU=0 Radius=1.65
  constraints (12):
    c: Diameter(g0) = 6
    c: Diameter(g1) = 6
    c: Diameter(g2) = 6
    c: Diameter(g3) = 6
    c: Diameter(g4) = 3.3
    c: Coincident(g4,g2)
    c: Diameter(g5) = 3.3
    c: Coincident(g5,g3)
    c: Diameter(g6) = 3.3
    c: Coincident(g6,g0)
    c: Diameter(g7) = 3.3
    c: Coincident(g7,g1)
FEATURE [PartDesign::Pad] Pad003
  BaseFeature = -> Pad
  Direction = (-1,0,2e-16)
  Length = 3.3
  Length2 = 10
  Placement = pos=(0,0,0) rot=(0,-1,0;1.5708rad)
  Profile = -> PCB_Sketch_f9e005
  ReferenceAxis = -> PCB_Sketch_f9e005 [N_Axis]
  Refine = true
  Suppressed = false
  Type = 0
FEATURE [Sketcher::SketchObject] Sketch  label="tindie"
  ArcFitTolerance = 1e-06
  AttachmentSupport = -> [XY_Plane001]
  FullyConstrained = true
  MakeInternals = false
  MapMode = 5
  sketch-geometry (4):
    g0: LineSegment StartX=0 StartY=0 StartZ=0 EndX=21 EndY=0 EndZ=0
    g1: LineSegment StartX=21 StartY=0 StartZ=0 EndX=21 EndY=28 EndZ=0
    g2: LineSegment StartX=21 StartY=28 StartZ=0 EndX=0 EndY=28 EndZ=0
    g3: LineSegment StartX=0 StartY=28 StartZ=0 EndX=0 EndY=0 EndZ=0
  constraints (11):
    c: Coincident(g0,g1)
    c: Coincident(g1,g2)
    c: Coincident(g2,g3)
    c: Coincident(g3,g0)
    c: Horizontal(g0)
    c: Horizontal(g2)
    c: Vertical(g1)
    c: Vertical(g3)
    c: Coincident(g0,g-1)
    c: DistanceY(g1,g1) = 28
    c: DistanceX(g2,g2) = 21
FEATURE [PartDesign::Pad] Pad015
  BaseFeature = -> Pad003
  Direction = (0,0,1)
  Length = 1.6
  Length2 = 10
  Placement = pos=(0,0,0) rot=(0,-1,0;1.5708rad)
  Profile = -> Sketch
  ReferenceAxis = -> Sketch [N_Axis]
  Refine = true
  Suppressed = false
  Type = 0
FEATURE [Sketcher::SketchObject] Sketch017
  ArcFitTolerance = 1e-06
  AttachmentSupport = -> [Pad015]
  FullyConstrained = false
  MakeInternals = false
  MapMode = 5
  Placement = pos=(1e-16,0,0) rot=(0.707107,0,0.707107;3.14159rad)
  sketch-geometry (2):
    g0: Circle CenterX=66.1396 CenterY=-28.2921 CenterZ=0 NormalX=0 NormalY=0 NormalZ=1 AngleXU=0 Radius=3.9
    g1: Circle CenterX=66.1396 CenterY=-28.2921 CenterZ=0 NormalX=0 NormalY=0 NormalZ=1 AngleXU=0 Radius=7
  constraints (3):
    c: Diameter(g0) = 7.8
    c: Diameter(g1) = 14
    c: Coincident(g1,g0)
FEATURE [PartDesign::Pad] Pad016
  BaseFeature = -> Pad015
  Direction = (1,0,-2e-16)
  Length = 6.5
  Length2 = 10
  Placement = pos=(0,0,0) rot=(0,-1,0;1.5708rad)
  Profile = -> Sketch017
  ReferenceAxis = -> Sketch017 [N_Axis]
  Refine = true
  Suppressed = false
  Type = 0
FEATURE [PartDesign::Body] Body  label="Left"
  AllowCompound = true
  Group = -> [PCB_Sketch_f9e005,PCB_Sketch_f9e4,Pad,Pad003,Sketch,Pad015,Sketch017,Pad016]
  Origin = -> Origin001
  Tip = -> Pad016
COMPONENT P9 — same part as P8; its construction recipe is shown at P8.
PROVENANCE & LICENSES
A FreeCAD (.FCStd) document from a public repository crawl; recipes are the document's own serialized feature recipes (and, for linked parts, companion documents' recipes).
License: gpl-3.0.
